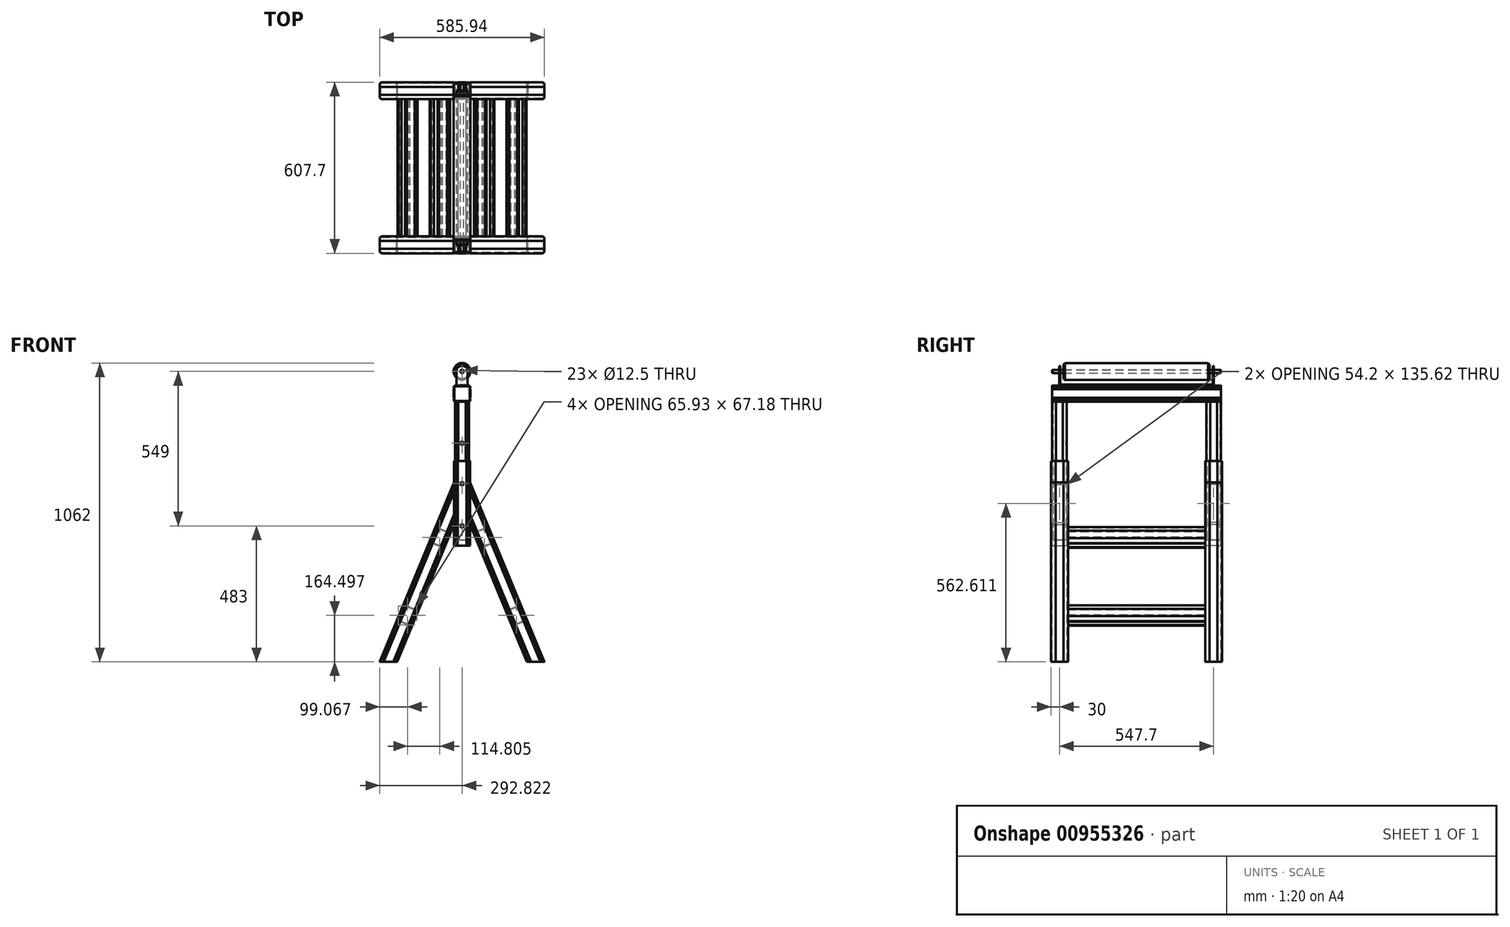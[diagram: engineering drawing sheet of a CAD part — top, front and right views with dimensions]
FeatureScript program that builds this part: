
annotation { "Feature Type Name" : "Feature", "Feature Type Description" : "" }
export const myFeature = defineFeature(function(context is Context, id is Id, definition is map)
    precondition{}
    {
        {
            var Q0;
            Q0=qCreatedBy(makeId("Front.planeOp"),FACE);
            var sketch = newSketch(context, id + "F0", { "sketchPlane" : qUnion([Q0])});
            skLineSegment(sketch, "E0", {"start": v(-264.27, 638) * mm, "end": v(0, 0) * mm});
            skLineSegment(sketch, "E1", {"start": v(0, 0) * mm, "end": v(-62.45, 0) * mm});
            skLineSegment(sketch, "E2", {"start": v(-62.45, 0) * mm, "end": v(-317.58, 615.92) * mm});
            skLineSegment(sketch, "E3", {"start": v(-317.58, 615.92) * mm, "end": v(-264.27, 638) * mm});
            skSolve(sketch);
        }
        {
            var Q0;
            Q0=makeQuery(id+"F0.imprint","IMPRINT",FACE,{"disambiguationData":[TD([[makeQuery(id+"F0.imprint","IMPRINT",EDGE,{"derivedFrom":sQuery(id+"F0.wireOp",EDGE,"E0")}),-1.0]])]});
            extrude(context, id + "F1", {"entities" : qUnion([Q0]), "depth" : 60 * mm, "offsetDistance" : 25 * mm});
        }
        {
            var Q0;
            Q0=makeQuery(id+"F1.opExtrude","CAP_EDGE",EDGE,{"disambiguationData":[OSD([sQuery(id+"F0.wireOp",EDGE,"E0")])],"isStart":false});
            var Q1;
            Q1=makeQuery(id+"F1.opExtrude","CAP_EDGE",EDGE,{"disambiguationData":[OSD([sQuery(id+"F0.wireOp",EDGE,"E0")])],"isStart":true});
            var Q2;
            Q2=makeQuery(id+"F1.opExtrude","CAP_EDGE",EDGE,{"disambiguationData":[OSD([sQuery(id+"F0.wireOp",EDGE,"E2")])],"isStart":true});
            var Q3;
            Q3=makeQuery(id+"F1.opExtrude","CAP_EDGE",EDGE,{"disambiguationData":[OSD([sQuery(id+"F0.wireOp",EDGE,"E2")])],"isStart":false});
            fillet(context, id + "F2", {"entities" : qUnion([Q0, Q1, Q2, Q3]), "radius" : 7.5 * mm, "tangentPropagation" : true, "allowEdgeOverflow" : false});
        }
        {
            var Q0;
            Q0=makeQuery(id+"F1.opExtrude","SWEPT_FACE",FACE,{"disambiguationData":[OSD([sQuery(id+"F0.wireOp",EDGE,"E3")])]});
            var sketch = newSketch(context, id + "F3", { "sketchPlane" : qUnion([Q0])});
            skArc(sketch, "E4.0", {"start": v(-50.2, -2.9) * mm, "mid": v(-53.45, -4.25) * mm, "end": v(-54.8, -7.5) * mm});
            skLineSegment(sketch, "E4.1", {"start": v(-54.8, -52.5) * mm, "end": v(-54.8, -7.5) * mm});
            skLineSegment(sketch, "E4.2", {"start": v(-50.2, -2.9) * mm, "end": v(-7.5, -2.9) * mm});
            skArc(sketch, "E4.3", {"start": v(-54.8, -52.5) * mm, "mid": v(-53.45, -55.75) * mm, "end": v(-50.2, -57.1) * mm});
            skArc(sketch, "E4.4", {"start": v(-2.9, -7.5) * mm, "mid": v(-4.25, -4.25) * mm, "end": v(-7.5, -2.9) * mm});
            skLineSegment(sketch, "E4.5", {"start": v(-2.9, -52.5) * mm, "end": v(-2.9, -7.5) * mm});
            skArc(sketch, "E4.6", {"start": v(-7.5, -57.1) * mm, "mid": v(-4.25, -55.75) * mm, "end": v(-2.9, -52.5) * mm});
            skLineSegment(sketch, "E4.7", {"start": v(-50.2, -57.1) * mm, "end": v(-7.5, -57.1) * mm});
            skLineSegment(sketch, "E5", {"start": v(-2.9, -7.5) * mm, "end": v(0, -7.5) * mm, "construction": true});
            skLineSegment(sketch, "E6", {"start": v(-2.9, -30) * mm, "end": v(0, -30) * mm, "construction": true});
            skLineSegment(sketch, "E7.0", {"start": v(-0.3, -44) * mm, "end": v(-0.3, -16) * mm});
            skLineSegment(sketch, "E8", {"start": v(-0.3, -16) * mm, "end": v(0, -16) * mm});
            skLineSegment(sketch, "E9", {"start": v(-0.3, -44) * mm, "end": v(0, -44) * mm});
            skLineSegment(sketch, "E10", {"start": v(-7.5, -57.1) * mm, "end": v(-7.5, -60) * mm, "construction": true});
            skLineSegment(sketch, "E11", {"start": v(-7.5, -60) * mm, "end": v(-8.5, -59) * mm});
            skLineSegment(sketch, "E12", {"start": v(-8.5, -59) * mm, "end": v(-9.5, -60) * mm});
            skLineSegment(sketch, "E13.1.0.0", {"start": v(-9.5, -60) * mm, "end": v(-10.5, -59) * mm});
            skLineSegment(sketch, "E13.1.0.1", {"start": v(-10.5, -59) * mm, "end": v(-11.5, -60) * mm});
            skLineSegment(sketch, "E13.2.0.0", {"start": v(-11.5, -60) * mm, "end": v(-12.5, -59) * mm});
            skLineSegment(sketch, "E13.2.0.1", {"start": v(-12.5, -59) * mm, "end": v(-13.5, -60) * mm});
            skLineSegment(sketch, "E13.direction1", {"start": v(-7.5, -60) * mm, "end": v(-9.5, -60) * mm, "construction": true});
            skLineSegment(sketch, "E14", {"start": v(-28.85, -60) * mm, "end": v(-28.85, -57.1) * mm, "construction": true});
            skLineSegment(sketch, "E15.MirrorCS", {"start": v(-50.2, -60) * mm, "end": v(-49.2, -59) * mm});
            skLineSegment(sketch, "E16.MirrorCS", {"start": v(-49.2, -59) * mm, "end": v(-48.2, -60) * mm});
            skLineSegment(sketch, "E17.MirrorCS", {"start": v(-48.2, -60) * mm, "end": v(-47.2, -59) * mm});
            skLineSegment(sketch, "E18.MirrorCS", {"start": v(-47.2, -59) * mm, "end": v(-46.2, -60) * mm});
            skLineSegment(sketch, "E19.MirrorCS", {"start": v(-46.2, -60) * mm, "end": v(-45.2, -59) * mm});
            skLineSegment(sketch, "E20.MirrorCS", {"start": v(-45.2, -59) * mm, "end": v(-44.2, -60) * mm});
            skLineSegment(sketch, "E21.MirrorCS", {"start": v(-57.4, -16) * mm, "end": v(-57.7, -16) * mm});
            skLineSegment(sketch, "E22.MirrorCS", {"start": v(-57.4, -44) * mm, "end": v(-57.4, -16) * mm});
            skLineSegment(sketch, "E23.MirrorCS", {"start": v(-57.4, -44) * mm, "end": v(-57.7, -44) * mm});
            skLineSegment(sketch, "E24.MirrorCS", {"start": v(-7.5, 0) * mm, "end": v(-8.5, -1) * mm});
            skLineSegment(sketch, "E25.MirrorCS", {"start": v(-8.5, -1) * mm, "end": v(-9.5, 0) * mm});
            skLineSegment(sketch, "E26.MirrorCS", {"start": v(-9.5, 0) * mm, "end": v(-10.5, -1) * mm});
            skLineSegment(sketch, "E27.MirrorCS", {"start": v(-10.5, -1) * mm, "end": v(-11.5, 0) * mm});
            skLineSegment(sketch, "E28.MirrorCS", {"start": v(-11.5, 0) * mm, "end": v(-12.5, -1) * mm});
            skLineSegment(sketch, "E29.MirrorCS", {"start": v(-12.5, -1) * mm, "end": v(-13.5, 0) * mm});
            skLineSegment(sketch, "E30.MirrorCS", {"start": v(-45.2, -1) * mm, "end": v(-44.2, 0) * mm});
            skLineSegment(sketch, "E31.MirrorCS", {"start": v(-46.2, 0) * mm, "end": v(-45.2, -1) * mm});
            skLineSegment(sketch, "E32.MirrorCS", {"start": v(-47.2, -1) * mm, "end": v(-46.2, 0) * mm});
            skLineSegment(sketch, "E33.MirrorCS", {"start": v(-48.2, 0) * mm, "end": v(-47.2, -1) * mm});
            skLineSegment(sketch, "E34.MirrorCS", {"start": v(-49.2, -1) * mm, "end": v(-48.2, 0) * mm});
            skLineSegment(sketch, "E35.MirrorCS", {"start": v(-50.2, 0) * mm, "end": v(-49.2, -1) * mm});
            skSolve(sketch);
        }
        {
            var Q0;
            {var subQ0=sQuery(id+"F3.wireOp",EDGE,"E24.MirrorCS");Q0=makeQuery(id+"F3.imprint","IMPRINT",FACE,{"disambiguationData":[TD([[makeQuery(id+"F3.imprint","IMPRINT",EDGE,{"derivedFrom":subQ0}),-1.0]])]});}
            var Q1;
            {var subQ0=sQuery(id+"F3.wireOp",EDGE,"E26.MirrorCS");Q1=makeQuery(id+"F3.imprint","IMPRINT",FACE,{"disambiguationData":[TD([[makeQuery(id+"F3.imprint","IMPRINT",EDGE,{"derivedFrom":subQ0}),-1.0]])]});}
            var Q2;
            {var subQ0=sQuery(id+"F3.wireOp",EDGE,"E28.MirrorCS");Q2=makeQuery(id+"F3.imprint","IMPRINT",FACE,{"disambiguationData":[TD([[makeQuery(id+"F3.imprint","IMPRINT",EDGE,{"derivedFrom":subQ0}),-1.0]])]});}
            var Q3;
            Q3=makeQuery(id+"F3.imprint","IMPRINT",FACE,{"disambiguationData":[TD([[makeQuery(id+"F3.imprint","IMPRINT",EDGE,{"derivedFrom":sQuery(id+"F3.wireOp",EDGE,"E4.0")}),1.0]])]});
            var Q4;
            {var subQ0=sQuery(id+"F3.wireOp",EDGE,"E30.MirrorCS");Q4=makeQuery(id+"F3.imprint","IMPRINT",FACE,{"disambiguationData":[TD([[makeQuery(id+"F3.imprint","IMPRINT",EDGE,{"derivedFrom":subQ0}),1.0]])]});}
            var Q5;
            {var subQ0=sQuery(id+"F3.wireOp",EDGE,"E32.MirrorCS");Q5=makeQuery(id+"F3.imprint","IMPRINT",FACE,{"disambiguationData":[TD([[makeQuery(id+"F3.imprint","IMPRINT",EDGE,{"derivedFrom":subQ0}),1.0]])]});}
            var Q6;
            {var subQ0=sQuery(id+"F3.wireOp",EDGE,"E34.MirrorCS");Q6=makeQuery(id+"F3.imprint","IMPRINT",FACE,{"disambiguationData":[TD([[makeQuery(id+"F3.imprint","IMPRINT",EDGE,{"derivedFrom":subQ0}),1.0]])]});}
            var Q7;
            {var subQ0=sQuery(id+"F3.wireOp",EDGE,"E21.MirrorCS");Q7=makeQuery(id+"F3.imprint","IMPRINT",FACE,{"disambiguationData":[TD([[makeQuery(id+"F3.imprint","IMPRINT",EDGE,{"derivedFrom":subQ0}),1.0]])]});}
            var Q8;
            {var subQ0=sQuery(id+"F3.wireOp",EDGE,"E15.MirrorCS");Q8=makeQuery(id+"F3.imprint","IMPRINT",FACE,{"disambiguationData":[TD([[makeQuery(id+"F3.imprint","IMPRINT",EDGE,{"derivedFrom":subQ0}),-1.0]])]});}
            var Q9;
            {var subQ0=sQuery(id+"F3.wireOp",EDGE,"E17.MirrorCS");Q9=makeQuery(id+"F3.imprint","IMPRINT",FACE,{"disambiguationData":[TD([[makeQuery(id+"F3.imprint","IMPRINT",EDGE,{"derivedFrom":subQ0}),-1.0]])]});}
            var Q10;
            {var subQ0=sQuery(id+"F3.wireOp",EDGE,"E19.MirrorCS");Q10=makeQuery(id+"F3.imprint","IMPRINT",FACE,{"disambiguationData":[TD([[makeQuery(id+"F3.imprint","IMPRINT",EDGE,{"derivedFrom":subQ0}),-1.0]])]});}
            var Q11;
            {var subQ0=sQuery(id+"F3.wireOp",EDGE,"E11");Q11=makeQuery(id+"F3.imprint","IMPRINT",FACE,{"disambiguationData":[TD([[makeQuery(id+"F3.imprint","IMPRINT",EDGE,{"derivedFrom":subQ0}),1.0]])]});}
            var Q12;
            {var subQ0=sQuery(id+"F3.wireOp",EDGE,"E13.1.0.0");Q12=makeQuery(id+"F3.imprint","IMPRINT",FACE,{"disambiguationData":[TD([[makeQuery(id+"F3.imprint","IMPRINT",EDGE,{"derivedFrom":subQ0}),1.0]])]});}
            var Q13;
            {var subQ0=sQuery(id+"F3.wireOp",EDGE,"E13.2.0.0");Q13=makeQuery(id+"F3.imprint","IMPRINT",FACE,{"disambiguationData":[TD([[makeQuery(id+"F3.imprint","IMPRINT",EDGE,{"derivedFrom":subQ0}),1.0]])]});}
            var Q14;
            Q14=makeQuery(id+"F3.imprint","IMPRINT",FACE,{"disambiguationData":[TD([[makeQuery(id+"F3.imprint","IMPRINT",EDGE,{"derivedFrom":sQuery(id+"F3.wireOp",EDGE,"E7.0")}),-1.0]])]});
            extrude(context, id + "F4", {"entities" : qUnion([Q0, Q1, Q2, Q3, Q4, Q5, Q6, Q7, Q8, Q9, Q10, Q11, Q12, Q13, Q14]), "operationType" : NewBodyOperationType.REMOVE, "endBound" : BoundingType.THROUGH_ALL, "oppositeDirection" : true, "depth" : 25 * mm, "offsetDistance" : 25 * mm});
        }
        {
            var Q0;
            Q0=makeQuery(id+"F1.opExtrude","CAP_FACE",FACE,{"disambiguationData":[OSD([sQuery(id+"F0.wireOp",EDGE,"E0"),sQuery(id+"F0.wireOp",EDGE,"E1"),sQuery(id+"F0.wireOp",EDGE,"E2"),sQuery(id+"F0.wireOp",EDGE,"E3")])],"isStart":false});
            var sketch = newSketch(context, id + "F5", { "sketchPlane" : qUnion([Q0])});
            skLineSegment(sketch, "E36", {"start": v(-317.58, 615.92) * mm, "end": v(-264.27, 638) * mm});
            skLineSegment(sketch, "E37", {"start": v(-264.27, 638) * mm, "end": v(-264.27, 487.22) * mm});
            skLineSegment(sketch, "E38", {"start": v(-264.27, 487.22) * mm, "end": v(-317.58, 615.92) * mm});
            skSolve(sketch);
        }
        {
            var Q0;
            Q0 = qSketchRegion(id + "F5", true);
            var Q1;
            Q1=makeQuery(id+"F1.opExtrude","CAP_FACE",FACE,{"disambiguationData":[OSD([sQuery(id+"F0.wireOp",EDGE,"E0"),sQuery(id+"F0.wireOp",EDGE,"E1"),sQuery(id+"F0.wireOp",EDGE,"E2"),sQuery(id+"F0.wireOp",EDGE,"E3")])],"isStart":true});
            extrude(context, id + "F6", {"entities" : qUnion([Q0]), "operationType" : NewBodyOperationType.REMOVE, "endBound" : BoundingType.UP_TO_SURFACE, "oppositeDirection" : true, "depth" : 25 * mm, "endBoundEntityFace" : qUnion([Q1]), "offsetDistance" : 25 * mm});
        }
        {
            var Q0;
            {var subQ0=sQuery(id+"F0.wireOp",EDGE,"E0");var subQ1=sQuery(id+"F0.wireOp",EDGE,"E3");Q0=makeQuery(id+"F6.boolean.opBoolean","MERGE",EDGE,{"derivedFrom":[makeQuery(id+"F4.boolean.opBoolean","SPLIT",EDGE,{"disambiguationData":[TD([makeQuery(id+"F4.opExtrude","SWEPT_FACE",FACE,{"disambiguationData":[OSD([sQuery(id+"F3.wireOp",EDGE,"E9")])]})])],"derivedFrom":makeQuery(id+"F1.opExtrude","SWEPT_EDGE",EDGE,{"disambiguationData":[OSD([subQ0,subQ1])]})})],"fromTools":[makeQuery(id+"F6.opExtrude","SWEPT_EDGE",EDGE,{"disambiguationData":[OSD([sQuery(id+"F5.wireOp",EDGE,"E36"),sQuery(id+"F5.wireOp",EDGE,"E37")])]})]});}
            cPlane(context, id + "F7", {"entities" : qUnion([Q0]), "cplaneType" : CPlaneType.LINE_ANGLE, "offset" : 25 * mm, "angle" : 0 * degree, "width" : 150 * mm, "height" : 150 * mm});
        }
        {
            var Q0;
            Q0=qCreatedBy(id+"F7.planeOp",FACE);
            cPlane(context, id + "F8", {"entities" : qUnion([Q0]), "cplaneType" : CPlaneType.OFFSET, "offset" : 75 * mm, "width" : 150 * mm, "height" : 150 * mm});
        }
        {
            var Q0;
            Q0=qCreatedBy(id+"F8.planeOp",FACE);
            var sketch = newSketch(context, id + "F9", { "sketchPlane" : qUnion([Q0])});
            skLineSegment(sketch, "E39", {"start": v(-321.97, -52.5) * mm, "end": v(-321.97, -44) * mm});
            skLineSegment(sketch, "E40", {"start": v(-321.97, -44) * mm, "end": v(-321.67, -44) * mm});
            skLineSegment(sketch, "E41", {"start": v(-321.67, -44) * mm, "end": v(-321.67, -30) * mm});
            skLineSegment(sketch, "E42", {"start": v(-321.67, -30) * mm, "end": v(-264.57, -30) * mm, "construction": true});
            skLineSegment(sketch, "E43", {"start": v(-264.57, -30) * mm, "end": v(-264.57, -44) * mm});
            skLineSegment(sketch, "E44", {"start": v(-264.57, -44) * mm, "end": v(-264.27, -44) * mm});
            skLineSegment(sketch, "E45", {"start": v(-264.27, -44) * mm, "end": v(-264.27, -52.5) * mm});
            skArc(sketch, "E46.filletArc", {"start": v(-271.77, -60) * mm, "mid": v(-266.46, -57.8) * mm, "end": v(-264.27, -52.5) * mm});
            skArc(sketch, "E47.filletArc", {"start": v(-321.97, -52.5) * mm, "mid": v(-319.77, -57.8) * mm, "end": v(-314.47, -60) * mm});
            skLineSegment(sketch, "E48", {"start": v(-277.77, -60) * mm, "end": v(-308.47, -60) * mm});
            skLineSegment(sketch, "E49", {"start": v(-271.77, -60) * mm, "end": v(-272.77, -59) * mm});
            skLineSegment(sketch, "E50", {"start": v(-272.77, -59) * mm, "end": v(-273.77, -60) * mm});
            skLineSegment(sketch, "E51.1.0.0", {"start": v(-273.77, -60) * mm, "end": v(-274.77, -59) * mm});
            skLineSegment(sketch, "E51.1.0.1", {"start": v(-274.77, -59) * mm, "end": v(-275.77, -60) * mm});
            skLineSegment(sketch, "E51.2.0.0", {"start": v(-275.77, -60) * mm, "end": v(-276.77, -59) * mm});
            skLineSegment(sketch, "E51.2.0.1", {"start": v(-276.77, -59) * mm, "end": v(-277.77, -60) * mm});
            skLineSegment(sketch, "E51.direction1", {"start": v(-271.77, -60) * mm, "end": v(-273.77, -60) * mm, "construction": true});
            skLineSegment(sketch, "E52", {"start": v(-314.47, -60) * mm, "end": v(-313.47, -59) * mm});
            skLineSegment(sketch, "E53", {"start": v(-313.47, -59) * mm, "end": v(-312.47, -60) * mm});
            skLineSegment(sketch, "E54.1.0.0", {"start": v(-312.47, -60) * mm, "end": v(-311.47, -59) * mm});
            skLineSegment(sketch, "E54.1.0.1", {"start": v(-311.47, -59) * mm, "end": v(-310.47, -60) * mm});
            skLineSegment(sketch, "E54.2.0.0", {"start": v(-310.47, -60) * mm, "end": v(-309.47, -59) * mm});
            skLineSegment(sketch, "E54.2.0.1", {"start": v(-309.47, -59) * mm, "end": v(-308.47, -60) * mm});
            skLineSegment(sketch, "E54.direction1", {"start": v(-314.47, -60) * mm, "end": v(-312.47, -60) * mm, "construction": true});
            skLineSegment(sketch, "E55", {"start": v(-318.77, -30) * mm, "end": v(-318.77, -52.6) * mm});
            skLineSegment(sketch, "E56", {"start": v(-314.27, -57.1) * mm, "end": v(-271.67, -57.1) * mm});
            skLineSegment(sketch, "E57", {"start": v(-267.17, -52.6) * mm, "end": v(-267.17, -30) * mm});
            skPoint(sketch, "E58.visualSharp", {"position": v(-318.77, -57.1) * mm});
            skArc(sketch, "E58.filletArc", {"start": v(-318.77, -52.6) * mm, "mid": v(-317.45, -55.78) * mm, "end": v(-314.27, -57.1) * mm});
            skPoint(sketch, "E59.visualSharp", {"position": v(-267.17, -57.1) * mm});
            skArc(sketch, "E59.filletArc", {"start": v(-271.67, -57.1) * mm, "mid": v(-268.49, -55.78) * mm, "end": v(-267.17, -52.6) * mm});
            skLineSegment(sketch, "E60.MirrorCS", {"start": v(-314.47, 0) * mm, "end": v(-312.47, 0) * mm, "construction": true});
            skLineSegment(sketch, "E61.MirrorCS", {"start": v(-313.47, -1) * mm, "end": v(-312.47, 0) * mm});
            skLineSegment(sketch, "E62.MirrorCS", {"start": v(-314.47, 0) * mm, "end": v(-313.47, -1) * mm});
            skLineSegment(sketch, "E63.MirrorCS", {"start": v(-264.57, -16) * mm, "end": v(-264.27, -16) * mm});
            skLineSegment(sketch, "E64.MirrorCS", {"start": v(-271.77, 0) * mm, "end": v(-272.77, -1) * mm});
            skLineSegment(sketch, "E65.MirrorCS", {"start": v(-273.77, 0) * mm, "end": v(-274.77, -1) * mm});
            skLineSegment(sketch, "E66.MirrorCS", {"start": v(-271.77, 0) * mm, "end": v(-273.77, 0) * mm, "construction": true});
            skLineSegment(sketch, "E67.MirrorCS", {"start": v(-312.47, 0) * mm, "end": v(-311.47, -1) * mm});
            skLineSegment(sketch, "E68.MirrorCS", {"start": v(-272.77, -1) * mm, "end": v(-273.77, 0) * mm});
            skLineSegment(sketch, "E69.MirrorCS", {"start": v(-321.97, -16) * mm, "end": v(-321.67, -16) * mm});
            skLineSegment(sketch, "E70.MirrorCS", {"start": v(-309.47, -1) * mm, "end": v(-308.47, 0) * mm});
            skLineSegment(sketch, "E71.MirrorCS", {"start": v(-276.77, -1) * mm, "end": v(-277.77, 0) * mm});
            skLineSegment(sketch, "E72.MirrorCS", {"start": v(-275.77, 0) * mm, "end": v(-276.77, -1) * mm});
            skLineSegment(sketch, "E73.MirrorCS", {"start": v(-310.47, 0) * mm, "end": v(-309.47, -1) * mm});
            skLineSegment(sketch, "E74.MirrorCS", {"start": v(-274.77, -1) * mm, "end": v(-275.77, 0) * mm});
            skLineSegment(sketch, "E75.MirrorCS", {"start": v(-311.47, -1) * mm, "end": v(-310.47, 0) * mm});
            skLineSegment(sketch, "E76.MirrorCS", {"start": v(-318.77, -30) * mm, "end": v(-318.77, -7.4) * mm});
            skArc(sketch, "E77.MirrorCS", {"start": v(-271.67, -2.9) * mm, "mid": v(-268.49, -4.22) * mm, "end": v(-267.17, -7.4) * mm});
            skArc(sketch, "E78.MirrorCS", {"start": v(-318.77, -7.4) * mm, "mid": v(-317.45, -4.22) * mm, "end": v(-314.27, -2.9) * mm});
            skPoint(sketch, "E79.MirrorP", {"position": v(-318.77, -2.9) * mm});
            skArc(sketch, "E80.MirrorCS", {"start": v(-271.77, 0) * mm, "mid": v(-266.46, -2.2) * mm, "end": v(-264.27, -7.5) * mm});
            skLineSegment(sketch, "E81.MirrorCS", {"start": v(-267.17, -7.4) * mm, "end": v(-267.17, -30) * mm});
            skLineSegment(sketch, "E82.MirrorCS", {"start": v(-321.67, -16) * mm, "end": v(-321.67, -30) * mm});
            skLineSegment(sketch, "E83.MirrorCS", {"start": v(-264.27, -16) * mm, "end": v(-264.27, -7.5) * mm});
            skPoint(sketch, "E84.MirrorP", {"position": v(-267.17, -2.9) * mm});
            skLineSegment(sketch, "E85.MirrorCS", {"start": v(-264.57, -30) * mm, "end": v(-264.57, -16) * mm});
            skLineSegment(sketch, "E86.MirrorCS", {"start": v(-314.27, -2.9) * mm, "end": v(-271.67, -2.9) * mm});
            skLineSegment(sketch, "E87.MirrorCS", {"start": v(-321.97, -7.5) * mm, "end": v(-321.97, -16) * mm});
            skArc(sketch, "E88.MirrorCS", {"start": v(-321.97, -7.5) * mm, "mid": v(-319.77, -2.2) * mm, "end": v(-314.47, 0) * mm});
            skLineSegment(sketch, "E89.MirrorCS", {"start": v(-277.77, 0) * mm, "end": v(-308.47, 0) * mm});
            skSolve(sketch);
        }
        {
            var Q0;
            Q0 = qSketchRegion(id + "F9", true);
            extrude(context, id + "F10", {"entities" : qUnion([Q0]), "oppositeDirection" : true, "depth" : 300 * mm, "offsetDistance" : 25 * mm});
        }
        {
            var Q0;
            Q0=makeQuery(id+"F10.opExtrude","SWEPT_FACE",FACE,{"disambiguationData":[OSD([sQuery(id+"F9.wireOp",EDGE,"E57"),sQuery(id+"F9.wireOp",EDGE,"E81.MirrorCS")])]});
            var Q1;
            Q1=makeQuery(id+"F10.opExtrude","SWEPT_FACE",FACE,{"disambiguationData":[OSD([sQuery(id+"F9.wireOp",EDGE,"E55"),sQuery(id+"F9.wireOp",EDGE,"E76.MirrorCS")])]});
            cPlane(context, id + "F11", {"entities" : qUnion([Q0, Q1]), "cplaneType" : CPlaneType.MID_PLANE, "offset" : 25 * mm, "width" : 150 * mm, "height" : 150 * mm});
        }
        {
            var Q0;
            Q0=makeQuery(id+"F1.opExtrude","SWEPT_BODY",BODY,{"disambiguationData":[OSD([sQuery(id+"F0.wireOp",EDGE,"E0"),sQuery(id+"F0.wireOp",EDGE,"E1"),sQuery(id+"F0.wireOp",EDGE,"E2"),sQuery(id+"F0.wireOp",EDGE,"E3")])]});
            var Q1;
            Q1=qCreatedBy(id+"F11.planeOp",FACE);
            mirror(context, id + "F12", {"entities" : qUnion([Q0]), "mirrorPlane" : qUnion([Q1])});
        }
        {
            var Q0;
            Q0=makeQuery(id+"F10.opExtrude","SWEPT_FACE",FACE,{"disambiguationData":[OSD([sQuery(id+"F9.wireOp",EDGE,"E89.MirrorCS")])]});
            var sketch = newSketch(context, id + "F13", { "sketchPlane" : qUnion([Q0])});
            skLineSegment(sketch, "E90", {"start": v(293.12, 713) * mm, "end": v(293.12, 413) * mm, "construction": true});
            skCircle(sketch, "E91", {"center": v(293.12, 633) * mm, "radius": 6.25 * mm});
            skCircle(sketch, "E92", {"center": v(293.12, 483) * mm, "radius": 6.25 * mm});
            skSolve(sketch);
        }
        {
            var Q0;
            Q0 = qSketchRegion(id + "F13", true);
            var Q1;
            Q1=makeQuery(id+"F10.opExtrude","SWEPT_FACE",FACE,{"disambiguationData":[OSD([sQuery(id+"F9.wireOp",EDGE,"E48")])]});
            extrude(context, id + "F14", {"entities" : qUnion([Q0]), "operationType" : NewBodyOperationType.REMOVE, "endBound" : BoundingType.UP_TO_SURFACE, "oppositeDirection" : true, "depth" : 25 * mm, "endBoundEntityFace" : qUnion([Q1]), "offsetDistance" : 25 * mm});
        }
        {
            var Q0;
            Q0=makeQuery(id+"F14.boolean.opBoolean","COPY",FACE,{"disambiguationData":[TD([makeQuery(id+"F10.opExtrude","SWEPT_FACE",FACE,{"disambiguationData":[OSD([sQuery(id+"F9.wireOp",EDGE,"E48")])]})])],"derivedFrom":makeQuery(id+"F14.opExtrude","SWEPT_FACE",FACE,{"disambiguationData":[OSD([sQuery(id+"F13.wireOp",EDGE,"E92")])]})});
            cPlane(context, id + "F15", {"entities" : qUnion([Q0]), "cplaneType" : CPlaneType.LINE_ANGLE, "offset" : 25 * mm, "angle" : 0 * degree, "width" : 150 * mm, "height" : 150 * mm});
        }
        {
            var Q0;
            Q0=qCreatedBy(id+"F15.planeOp",FACE);
            cPlane(context, id + "F16", {"entities" : qUnion([Q0]), "cplaneType" : CPlaneType.OFFSET, "offset" : 50 * mm, "width" : 150 * mm, "height" : 150 * mm});
        }
        {
            var Q0;
            Q0=qCreatedBy(id+"F16.planeOp",FACE);
            var sketch = newSketch(context, id + "F17", { "sketchPlane" : qUnion([Q0])});
            skLineSegment(sketch, "E93", {"start": v(-293.12, 0) * mm, "end": v(-293.12, 60) * mm, "construction": true});
            skLineSegment(sketch, "E94", {"start": v(-293.12, 56.15) * mm, "end": v(-306.87, 56.15) * mm});
            skLineSegment(sketch, "E95", {"start": v(-318.37, 48.65) * mm, "end": v(-318.37, 42.15) * mm});
            skLineSegment(sketch, "E96", {"start": v(-306.87, 3.85) * mm, "end": v(-293.12, 3.85) * mm});
            skPoint(sketch, "E97.visualSharp", {"position": v(-318.37, 56.15) * mm});
            skArc(sketch, "E97.filletArc", {"start": v(-310.87, 56.15) * mm, "mid": v(-316.17, 53.95) * mm, "end": v(-318.37, 48.65) * mm});
            skPoint(sketch, "E98.visualSharp", {"position": v(-318.37, 3.85) * mm});
            skArc(sketch, "E98.filletArc", {"start": v(-318.37, 11.35) * mm, "mid": v(-316.17, 6.05) * mm, "end": v(-310.87, 3.85) * mm});
            skLineSegment(sketch, "E99", {"start": v(-310.87, 56.15) * mm, "end": v(-309.87, 55.15) * mm});
            skLineSegment(sketch, "E100", {"start": v(-309.87, 55.15) * mm, "end": v(-308.87, 56.15) * mm});
            skLineSegment(sketch, "E101.1.0.0", {"start": v(-308.87, 56.15) * mm, "end": v(-307.87, 55.15) * mm});
            skLineSegment(sketch, "E101.1.0.1", {"start": v(-307.87, 55.15) * mm, "end": v(-306.87, 56.15) * mm});
            skLineSegment(sketch, "E101.direction1", {"start": v(-309.87, 55.15) * mm, "end": v(-307.87, 55.15) * mm, "construction": true});
            skLineSegment(sketch, "E102", {"start": v(-310.87, 3.85) * mm, "end": v(-309.87, 4.85) * mm});
            skLineSegment(sketch, "E103", {"start": v(-309.87, 4.85) * mm, "end": v(-308.87, 3.85) * mm});
            skLineSegment(sketch, "E104.1.0.0", {"start": v(-308.87, 3.85) * mm, "end": v(-307.87, 4.85) * mm});
            skLineSegment(sketch, "E104.1.0.1", {"start": v(-307.87, 4.85) * mm, "end": v(-306.87, 3.85) * mm});
            skLineSegment(sketch, "E104.direction1", {"start": v(-310.87, 3.85) * mm, "end": v(-308.87, 3.85) * mm, "construction": true});
            skLineSegment(sketch, "E105", {"start": v(-293.12, 53.25) * mm, "end": v(-310.97, 53.25) * mm});
            skLineSegment(sketch, "E106", {"start": v(-315.47, 48.75) * mm, "end": v(-315.47, 11.25) * mm});
            skLineSegment(sketch, "E107", {"start": v(-310.97, 6.75) * mm, "end": v(-293.12, 6.75) * mm});
            skPoint(sketch, "E108.visualSharp", {"position": v(-315.47, 53.25) * mm});
            skArc(sketch, "E108.filletArc", {"start": v(-310.97, 53.25) * mm, "mid": v(-314.15, 51.93) * mm, "end": v(-315.47, 48.75) * mm});
            skPoint(sketch, "E109.visualSharp", {"position": v(-315.47, 6.75) * mm});
            skArc(sketch, "E109.filletArc", {"start": v(-315.47, 11.25) * mm, "mid": v(-314.15, 8.07) * mm, "end": v(-310.97, 6.75) * mm});
            skLineSegment(sketch, "E110", {"start": v(-306.87, 0) * mm, "end": v(-306.87, 56.15) * mm, "construction": true});
            skLineSegment(sketch, "E111", {"start": v(-306.87, 60) * mm, "end": v(-306.87, 3.85) * mm, "construction": true});
            skLineSegment(sketch, "E112.MirrorCS", {"start": v(-275.37, 3.85) * mm, "end": v(-277.37, 3.85) * mm, "construction": true});
            skLineSegment(sketch, "E113.MirrorCS", {"start": v(-275.37, 56.15) * mm, "end": v(-276.37, 55.15) * mm});
            skLineSegment(sketch, "E114.MirrorCS", {"start": v(-277.37, 3.85) * mm, "end": v(-278.37, 4.85) * mm});
            skLineSegment(sketch, "E115.MirrorCS", {"start": v(-276.37, 55.15) * mm, "end": v(-278.37, 55.15) * mm, "construction": true});
            skLineSegment(sketch, "E116.MirrorCS", {"start": v(-276.37, 55.15) * mm, "end": v(-277.37, 56.15) * mm});
            skLineSegment(sketch, "E117.MirrorCS", {"start": v(-278.37, 55.15) * mm, "end": v(-279.37, 56.15) * mm});
            skLineSegment(sketch, "E118.MirrorCS", {"start": v(-278.37, 4.85) * mm, "end": v(-279.37, 3.85) * mm});
            skLineSegment(sketch, "E119.MirrorCS", {"start": v(-277.37, 56.15) * mm, "end": v(-278.37, 55.15) * mm});
            skLineSegment(sketch, "E120.MirrorCS", {"start": v(-276.37, 4.85) * mm, "end": v(-277.37, 3.85) * mm});
            skLineSegment(sketch, "E121.MirrorCS", {"start": v(-275.37, 3.85) * mm, "end": v(-276.37, 4.85) * mm});
            skLineSegment(sketch, "E122.MirrorCS", {"start": v(-279.37, 60) * mm, "end": v(-279.37, 3.85) * mm, "construction": true});
            skLineSegment(sketch, "E123.MirrorCS", {"start": v(-279.37, 0) * mm, "end": v(-279.37, 56.15) * mm, "construction": true});
            skLineSegment(sketch, "E124.MirrorCS", {"start": v(-293.12, 56.15) * mm, "end": v(-279.37, 56.15) * mm});
            skLineSegment(sketch, "E125.MirrorCS", {"start": v(-267.87, 48.65) * mm, "end": v(-267.87, 42.15) * mm});
            skPoint(sketch, "E126.MirrorP", {"position": v(-267.87, 56.15) * mm});
            skArc(sketch, "E127.MirrorCS", {"start": v(-270.77, 11.25) * mm, "mid": v(-272.09, 8.07) * mm, "end": v(-275.27, 6.75) * mm});
            skArc(sketch, "E128.MirrorCS", {"start": v(-267.87, 11.35) * mm, "mid": v(-270.06, 6.05) * mm, "end": v(-275.37, 3.85) * mm});
            skArc(sketch, "E129.MirrorCS", {"start": v(-275.37, 56.15) * mm, "mid": v(-270.06, 53.95) * mm, "end": v(-267.87, 48.65) * mm});
            skLineSegment(sketch, "E130.MirrorCS", {"start": v(-275.27, 6.75) * mm, "end": v(-293.12, 6.75) * mm});
            skPoint(sketch, "E131.MirrorP", {"position": v(-267.87, 3.85) * mm});
            skPoint(sketch, "E132.MirrorP", {"position": v(-270.77, 6.75) * mm});
            skPoint(sketch, "E133.MirrorP", {"position": v(-270.77, 53.25) * mm});
            skArc(sketch, "E134.MirrorCS", {"start": v(-275.27, 53.25) * mm, "mid": v(-272.09, 51.93) * mm, "end": v(-270.77, 48.75) * mm});
            skLineSegment(sketch, "E135.MirrorCS", {"start": v(-293.12, 53.25) * mm, "end": v(-275.27, 53.25) * mm});
            skLineSegment(sketch, "E136.MirrorCS", {"start": v(-270.77, 48.75) * mm, "end": v(-270.77, 11.25) * mm});
            skLineSegment(sketch, "E137.MirrorCS", {"start": v(-279.37, 3.85) * mm, "end": v(-293.12, 3.85) * mm});
            skLineSegment(sketch, "E138", {"start": v(-318.37, 17.85) * mm, "end": v(-318.12, 17.85) * mm});
            skLineSegment(sketch, "E139", {"start": v(-318.12, 17.85) * mm, "end": v(-318.12, 42.15) * mm});
            skLineSegment(sketch, "E140", {"start": v(-318.12, 42.15) * mm, "end": v(-318.37, 42.15) * mm});
            skLineSegment(sketch, "E141.trimOffspring", {"start": v(-318.37, 17.85) * mm, "end": v(-318.37, 11.35) * mm});
            skLineSegment(sketch, "E142.MirrorCS", {"start": v(-267.87, 17.85) * mm, "end": v(-268.12, 17.85) * mm});
            skLineSegment(sketch, "E143.MirrorCS", {"start": v(-268.12, 17.85) * mm, "end": v(-268.12, 42.15) * mm});
            skLineSegment(sketch, "E144.MirrorCS", {"start": v(-268.12, 42.15) * mm, "end": v(-267.87, 42.15) * mm});
            skLineSegment(sketch, "E145.trimOffspring", {"start": v(-267.87, 17.85) * mm, "end": v(-267.87, 11.35) * mm});
            skSolve(sketch);
        }
        {
            var Q0;
            Q0 = qSketchRegion(id + "F17", true);
            extrude(context, id + "F18", {"entities" : qUnion([Q0]), "oppositeDirection" : true, "depth" : 491.3 * mm, "offsetDistance" : 25 * mm});
        }
        {
            var Q0;
            Q0=makeQuery(id+"F18.opExtrude","SWEPT_FACE",FACE,{"disambiguationData":[OSD([sQuery(id+"F17.wireOp",EDGE,"E96"),sQuery(id+"F17.wireOp",EDGE,"E137.MirrorCS")])]});
            var sketch = newSketch(context, id + "F19", { "sketchPlane" : qUnion([Q0])});
            skCircle(sketch, "E146", {"center": v(293.12, 633) * mm, "radius": 6.25 * mm});
            skCircle(sketch, "E147", {"center": v(293.12, 483) * mm, "radius": 6.25 * mm});
            skCircle(sketch, "E148", {"center": v(293.12, 776.75) * mm, "radius": 6.25 * mm});
            skSolve(sketch);
        }
        {
            var Q0;
            Q0 = qSketchRegion(id + "F19", true);
            var Q1;
            Q1=makeQuery(id+"F18.opExtrude","SWEPT_FACE",FACE,{"disambiguationData":[OSD([sQuery(id+"F17.wireOp",EDGE,"E94"),sQuery(id+"F17.wireOp",EDGE,"E124.MirrorCS")])]});
            extrude(context, id + "F20", {"entities" : qUnion([Q0]), "operationType" : NewBodyOperationType.REMOVE, "endBound" : BoundingType.UP_TO_SURFACE, "oppositeDirection" : true, "depth" : 25 * mm, "endBoundEntityFace" : qUnion([Q1]), "offsetDistance" : 25 * mm});
        }
        {
            var Q0;
            Q0=makeQuery(id+"F18.opExtrude","SWEPT_FACE",FACE,{"disambiguationData":[OSD([sQuery(id+"F17.wireOp",EDGE,"E96"),sQuery(id+"F17.wireOp",EDGE,"E137.MirrorCS")])]});
            var sketch = newSketch(context, id + "F21", { "sketchPlane" : qUnion([Q0])});
            skLineSegment(sketch, "E149", {"start": v(293.12, 981.7) * mm, "end": v(293.12, 924.6) * mm, "construction": true});
            skLineSegment(sketch, "E150", {"start": v(279.12, 982) * mm, "end": v(270.62, 982) * mm});
            skLineSegment(sketch, "E151", {"start": v(263.12, 968.5) * mm, "end": v(263.12, 937.8) * mm});
            skLineSegment(sketch, "E152", {"start": v(270.62, 924.3) * mm, "end": v(279.12, 924.3) * mm});
            skPoint(sketch, "E153.visualSharp", {"position": v(263.12, 982) * mm});
            skArc(sketch, "E153.filletArc", {"start": v(270.62, 982) * mm, "mid": v(265.31, 979.8) * mm, "end": v(263.12, 974.5) * mm});
            skPoint(sketch, "E154.visualSharp", {"position": v(263.12, 924.3) * mm});
            skArc(sketch, "E154.filletArc", {"start": v(263.12, 931.8) * mm, "mid": v(265.31, 926.5) * mm, "end": v(270.62, 924.3) * mm});
            skLineSegment(sketch, "E155", {"start": v(263.12, 974.5) * mm, "end": v(264.12, 973.5) * mm});
            skLineSegment(sketch, "E156", {"start": v(264.12, 973.5) * mm, "end": v(263.12, 972.5) * mm});
            skLineSegment(sketch, "E157.0.1.0", {"start": v(263.12, 972.5) * mm, "end": v(264.12, 971.5) * mm});
            skLineSegment(sketch, "E157.0.1.1", {"start": v(264.12, 971.5) * mm, "end": v(263.12, 970.5) * mm});
            skLineSegment(sketch, "E157.0.2.0", {"start": v(263.12, 970.5) * mm, "end": v(264.12, 969.5) * mm});
            skLineSegment(sketch, "E157.0.2.1", {"start": v(264.12, 969.5) * mm, "end": v(263.12, 968.5) * mm});
            skLineSegment(sketch, "E157.direction1", {"start": v(264.12, 973.5) * mm, "end": v(289.12, 973.5) * mm, "construction": true});
            skLineSegment(sketch, "E157.direction2", {"start": v(264.12, 973.5) * mm, "end": v(264.12, 971.5) * mm, "construction": true});
            skLineSegment(sketch, "E158", {"start": v(263.12, 931.8) * mm, "end": v(264.12, 932.8) * mm});
            skLineSegment(sketch, "E159", {"start": v(264.12, 932.8) * mm, "end": v(263.12, 933.8) * mm});
            skLineSegment(sketch, "E160.0.1.0", {"start": v(263.12, 933.8) * mm, "end": v(264.12, 934.8) * mm});
            skLineSegment(sketch, "E160.0.1.1", {"start": v(264.12, 934.8) * mm, "end": v(263.12, 935.8) * mm});
            skLineSegment(sketch, "E160.0.2.0", {"start": v(263.12, 935.8) * mm, "end": v(264.12, 936.8) * mm});
            skLineSegment(sketch, "E160.0.2.1", {"start": v(264.12, 936.8) * mm, "end": v(263.12, 937.8) * mm});
            skLineSegment(sketch, "E160.direction1", {"start": v(263.12, 931.8) * mm, "end": v(288.12, 931.8) * mm, "construction": true});
            skLineSegment(sketch, "E160.direction2", {"start": v(263.12, 931.8) * mm, "end": v(263.12, 933.8) * mm, "construction": true});
            skLineSegment(sketch, "E161", {"start": v(293.12, 981.7) * mm, "end": v(279.12, 981.7) * mm});
            skLineSegment(sketch, "E162", {"start": v(279.12, 981.7) * mm, "end": v(279.12, 982) * mm});
            skLineSegment(sketch, "E163", {"start": v(293.12, 924.6) * mm, "end": v(279.12, 924.6) * mm});
            skLineSegment(sketch, "E164", {"start": v(279.12, 924.6) * mm, "end": v(279.12, 924.3) * mm});
            skPoint(sketch, "E165.orphan", {"position": v(293.12, 924.3) * mm});
            skPoint(sketch, "E166.orphan", {"position": v(293.12, 982) * mm});
            skLineSegment(sketch, "E167", {"start": v(266.02, 974.3) * mm, "end": v(266.02, 932) * mm});
            skLineSegment(sketch, "E168", {"start": v(270.52, 927.5) * mm, "end": v(293.12, 927.5) * mm});
            skLineSegment(sketch, "E169", {"start": v(270.52, 978.8) * mm, "end": v(293.12, 978.8) * mm});
            skPoint(sketch, "E170.visualSharp", {"position": v(266.02, 978.8) * mm});
            skArc(sketch, "E170.filletArc", {"start": v(270.52, 978.8) * mm, "mid": v(267.34, 977.48) * mm, "end": v(266.02, 974.3) * mm});
            skPoint(sketch, "E171.visualSharp", {"position": v(266.02, 927.5) * mm});
            skArc(sketch, "E171.filletArc", {"start": v(266.02, 932) * mm, "mid": v(267.34, 928.82) * mm, "end": v(270.52, 927.5) * mm});
            skLineSegment(sketch, "E172.MirrorCS", {"start": v(322.12, 932.8) * mm, "end": v(323.12, 933.8) * mm});
            skLineSegment(sketch, "E173.MirrorCS", {"start": v(323.12, 931.8) * mm, "end": v(323.12, 933.8) * mm, "construction": true});
            skLineSegment(sketch, "E174.MirrorCS", {"start": v(322.12, 971.5) * mm, "end": v(323.12, 970.5) * mm});
            skLineSegment(sketch, "E175.MirrorCS", {"start": v(323.12, 931.8) * mm, "end": v(322.12, 932.8) * mm});
            skLineSegment(sketch, "E176.MirrorCS", {"start": v(323.12, 933.8) * mm, "end": v(322.12, 934.8) * mm});
            skLineSegment(sketch, "E177.MirrorCS", {"start": v(307.12, 981.7) * mm, "end": v(307.12, 982) * mm});
            skLineSegment(sketch, "E178.MirrorCS", {"start": v(322.12, 969.5) * mm, "end": v(323.12, 968.5) * mm});
            skLineSegment(sketch, "E179.MirrorCS", {"start": v(323.12, 972.5) * mm, "end": v(322.12, 971.5) * mm});
            skLineSegment(sketch, "E180.MirrorCS", {"start": v(322.12, 973.5) * mm, "end": v(323.12, 972.5) * mm});
            skLineSegment(sketch, "E181.MirrorCS", {"start": v(322.12, 973.5) * mm, "end": v(322.12, 971.5) * mm, "construction": true});
            skLineSegment(sketch, "E182.MirrorCS", {"start": v(323.12, 970.5) * mm, "end": v(322.12, 969.5) * mm});
            skLineSegment(sketch, "E183.MirrorCS", {"start": v(323.12, 974.5) * mm, "end": v(322.12, 973.5) * mm});
            skLineSegment(sketch, "E184.MirrorCS", {"start": v(323.12, 935.8) * mm, "end": v(322.12, 936.8) * mm});
            skLineSegment(sketch, "E185.MirrorCS", {"start": v(322.12, 934.8) * mm, "end": v(323.12, 935.8) * mm});
            skArc(sketch, "E186.MirrorCS", {"start": v(315.72, 978.8) * mm, "mid": v(318.9, 977.48) * mm, "end": v(320.22, 974.3) * mm});
            skLineSegment(sketch, "E187.MirrorCS", {"start": v(322.12, 936.8) * mm, "end": v(323.12, 937.8) * mm});
            skArc(sketch, "E188.MirrorCS", {"start": v(320.22, 932) * mm, "mid": v(318.9, 928.82) * mm, "end": v(315.72, 927.5) * mm});
            skLineSegment(sketch, "E189.MirrorCS", {"start": v(307.12, 924.6) * mm, "end": v(307.12, 924.3) * mm});
            skArc(sketch, "E190.MirrorCS", {"start": v(323.12, 931.8) * mm, "mid": v(320.92, 926.5) * mm, "end": v(315.62, 924.3) * mm});
            skArc(sketch, "E191.MirrorCS", {"start": v(315.62, 982) * mm, "mid": v(320.92, 979.8) * mm, "end": v(323.12, 974.5) * mm});
            skLineSegment(sketch, "E192.MirrorCS", {"start": v(322.12, 973.5) * mm, "end": v(297.12, 973.5) * mm, "construction": true});
            skPoint(sketch, "E193.MirrorP", {"position": v(320.22, 927.5) * mm});
            skLineSegment(sketch, "E194.MirrorCS", {"start": v(315.72, 927.5) * mm, "end": v(293.12, 927.5) * mm});
            skLineSegment(sketch, "E195.MirrorCS", {"start": v(320.22, 974.3) * mm, "end": v(320.22, 932) * mm});
            skLineSegment(sketch, "E196.MirrorCS", {"start": v(293.12, 981.7) * mm, "end": v(307.12, 981.7) * mm});
            skLineSegment(sketch, "E197.MirrorCS", {"start": v(323.12, 968.5) * mm, "end": v(323.12, 937.8) * mm});
            skLineSegment(sketch, "E198.MirrorCS", {"start": v(323.12, 931.8) * mm, "end": v(298.12, 931.8) * mm, "construction": true});
            skLineSegment(sketch, "E199.MirrorCS", {"start": v(315.62, 924.3) * mm, "end": v(307.12, 924.3) * mm});
            skPoint(sketch, "E200.MirrorP", {"position": v(323.12, 982) * mm});
            skLineSegment(sketch, "E201.MirrorCS", {"start": v(307.12, 982) * mm, "end": v(315.62, 982) * mm});
            skLineSegment(sketch, "E202.MirrorCS", {"start": v(293.12, 924.6) * mm, "end": v(307.12, 924.6) * mm});
            skLineSegment(sketch, "E203.MirrorCS", {"start": v(315.72, 978.8) * mm, "end": v(293.12, 978.8) * mm});
            skPoint(sketch, "E204.MirrorP", {"position": v(320.22, 978.8) * mm});
            skPoint(sketch, "E205.MirrorP", {"position": v(323.12, 924.3) * mm});
            skSolve(sketch);
        }
        {
            var Q0;
            Q0=makeQuery(id+"F21.imprint","IMPRINT",FACE,{"disambiguationData":[TD([[makeQuery(id+"F21.imprint","IMPRINT",EDGE,{"derivedFrom":sQuery(id+"F21.wireOp",EDGE,"E150")}),1.0]])]});
            extrude(context, id + "F22", {"entities" : qUnion([Q0]), "oppositeDirection" : true, "depth" : 600 * mm, "offsetDistance" : 25 * mm});
        }
        {
            var Q0;
            Q0=makeQuery(id+"F22.opExtrude","CAP_FACE",FACE,{"disambiguationData":[OSD([sQuery(id+"F21.wireOp",EDGE,"E150"),sQuery(id+"F21.wireOp",EDGE,"E151"),sQuery(id+"F21.wireOp",EDGE,"E152"),sQuery(id+"F21.wireOp",EDGE,"E153.filletArc"),sQuery(id+"F21.wireOp",EDGE,"E154.filletArc"),sQuery(id+"F21.wireOp",EDGE,"E155"),sQuery(id+"F21.wireOp",EDGE,"E156"),sQuery(id+"F21.wireOp",EDGE,"E157.0.1.0"),sQuery(id+"F21.wireOp",EDGE,"E157.0.1.1"),sQuery(id+"F21.wireOp",EDGE,"E157.0.2.0"),sQuery(id+"F21.wireOp",EDGE,"E157.0.2.1"),sQuery(id+"F21.wireOp",EDGE,"E158"),sQuery(id+"F21.wireOp",EDGE,"E159"),sQuery(id+"F21.wireOp",EDGE,"E160.0.1.0"),sQuery(id+"F21.wireOp",EDGE,"E160.0.1.1"),sQuery(id+"F21.wireOp",EDGE,"E160.0.2.0"),sQuery(id+"F21.wireOp",EDGE,"E160.0.2.1"),sQuery(id+"F21.wireOp",EDGE,"E161"),sQuery(id+"F21.wireOp",EDGE,"E162"),sQuery(id+"F21.wireOp",EDGE,"E163"),sQuery(id+"F21.wireOp",EDGE,"E164"),sQuery(id+"F21.wireOp",EDGE,"E167"),sQuery(id+"F21.wireOp",EDGE,"E168"),sQuery(id+"F21.wireOp",EDGE,"E169"),sQuery(id+"F21.wireOp",EDGE,"E170.filletArc"),sQuery(id+"F21.wireOp",EDGE,"E171.filletArc"),sQuery(id+"F21.wireOp",EDGE,"E172.MirrorCS"),sQuery(id+"F21.wireOp",EDGE,"E174.MirrorCS"),sQuery(id+"F21.wireOp",EDGE,"E175.MirrorCS"),sQuery(id+"F21.wireOp",EDGE,"E176.MirrorCS"),sQuery(id+"F21.wireOp",EDGE,"E177.MirrorCS"),sQuery(id+"F21.wireOp",EDGE,"E178.MirrorCS"),sQuery(id+"F21.wireOp",EDGE,"E179.MirrorCS"),sQuery(id+"F21.wireOp",EDGE,"E180.MirrorCS"),sQuery(id+"F21.wireOp",EDGE,"E182.MirrorCS"),sQuery(id+"F21.wireOp",EDGE,"E183.MirrorCS"),sQuery(id+"F21.wireOp",EDGE,"E184.MirrorCS"),sQuery(id+"F21.wireOp",EDGE,"E185.MirrorCS"),sQuery(id+"F21.wireOp",EDGE,"E186.MirrorCS"),sQuery(id+"F21.wireOp",EDGE,"E187.MirrorCS"),sQuery(id+"F21.wireOp",EDGE,"E188.MirrorCS"),sQuery(id+"F21.wireOp",EDGE,"E189.MirrorCS"),sQuery(id+"F21.wireOp",EDGE,"E190.MirrorCS"),sQuery(id+"F21.wireOp",EDGE,"E191.MirrorCS"),sQuery(id+"F21.wireOp",EDGE,"E194.MirrorCS"),sQuery(id+"F21.wireOp",EDGE,"E195.MirrorCS"),sQuery(id+"F21.wireOp",EDGE,"E196.MirrorCS"),sQuery(id+"F21.wireOp",EDGE,"E197.MirrorCS"),sQuery(id+"F21.wireOp",EDGE,"E199.MirrorCS"),sQuery(id+"F21.wireOp",EDGE,"E201.MirrorCS"),sQuery(id+"F21.wireOp",EDGE,"E202.MirrorCS"),sQuery(id+"F21.wireOp",EDGE,"E203.MirrorCS")])],"isStart":false});
            var Q1;
            Q1=makeQuery(id+"F22.opExtrude","CAP_FACE",FACE,{"disambiguationData":[OSD([sQuery(id+"F21.wireOp",EDGE,"E150"),sQuery(id+"F21.wireOp",EDGE,"E151"),sQuery(id+"F21.wireOp",EDGE,"E152"),sQuery(id+"F21.wireOp",EDGE,"E153.filletArc"),sQuery(id+"F21.wireOp",EDGE,"E154.filletArc"),sQuery(id+"F21.wireOp",EDGE,"E155"),sQuery(id+"F21.wireOp",EDGE,"E156"),sQuery(id+"F21.wireOp",EDGE,"E157.0.1.0"),sQuery(id+"F21.wireOp",EDGE,"E157.0.1.1"),sQuery(id+"F21.wireOp",EDGE,"E157.0.2.0"),sQuery(id+"F21.wireOp",EDGE,"E157.0.2.1"),sQuery(id+"F21.wireOp",EDGE,"E158"),sQuery(id+"F21.wireOp",EDGE,"E159"),sQuery(id+"F21.wireOp",EDGE,"E160.0.1.0"),sQuery(id+"F21.wireOp",EDGE,"E160.0.1.1"),sQuery(id+"F21.wireOp",EDGE,"E160.0.2.0"),sQuery(id+"F21.wireOp",EDGE,"E160.0.2.1"),sQuery(id+"F21.wireOp",EDGE,"E161"),sQuery(id+"F21.wireOp",EDGE,"E162"),sQuery(id+"F21.wireOp",EDGE,"E163"),sQuery(id+"F21.wireOp",EDGE,"E164"),sQuery(id+"F21.wireOp",EDGE,"E167"),sQuery(id+"F21.wireOp",EDGE,"E168"),sQuery(id+"F21.wireOp",EDGE,"E169"),sQuery(id+"F21.wireOp",EDGE,"E170.filletArc"),sQuery(id+"F21.wireOp",EDGE,"E171.filletArc"),sQuery(id+"F21.wireOp",EDGE,"E172.MirrorCS"),sQuery(id+"F21.wireOp",EDGE,"E174.MirrorCS"),sQuery(id+"F21.wireOp",EDGE,"E175.MirrorCS"),sQuery(id+"F21.wireOp",EDGE,"E176.MirrorCS"),sQuery(id+"F21.wireOp",EDGE,"E177.MirrorCS"),sQuery(id+"F21.wireOp",EDGE,"E178.MirrorCS"),sQuery(id+"F21.wireOp",EDGE,"E179.MirrorCS"),sQuery(id+"F21.wireOp",EDGE,"E180.MirrorCS"),sQuery(id+"F21.wireOp",EDGE,"E182.MirrorCS"),sQuery(id+"F21.wireOp",EDGE,"E183.MirrorCS"),sQuery(id+"F21.wireOp",EDGE,"E184.MirrorCS"),sQuery(id+"F21.wireOp",EDGE,"E185.MirrorCS"),sQuery(id+"F21.wireOp",EDGE,"E186.MirrorCS"),sQuery(id+"F21.wireOp",EDGE,"E187.MirrorCS"),sQuery(id+"F21.wireOp",EDGE,"E188.MirrorCS"),sQuery(id+"F21.wireOp",EDGE,"E189.MirrorCS"),sQuery(id+"F21.wireOp",EDGE,"E190.MirrorCS"),sQuery(id+"F21.wireOp",EDGE,"E191.MirrorCS"),sQuery(id+"F21.wireOp",EDGE,"E194.MirrorCS"),sQuery(id+"F21.wireOp",EDGE,"E195.MirrorCS"),sQuery(id+"F21.wireOp",EDGE,"E196.MirrorCS"),sQuery(id+"F21.wireOp",EDGE,"E197.MirrorCS"),sQuery(id+"F21.wireOp",EDGE,"E199.MirrorCS"),sQuery(id+"F21.wireOp",EDGE,"E201.MirrorCS"),sQuery(id+"F21.wireOp",EDGE,"E202.MirrorCS"),sQuery(id+"F21.wireOp",EDGE,"E203.MirrorCS")])],"isStart":true});
            cPlane(context, id + "F23", {"entities" : qUnion([Q0, Q1]), "cplaneType" : CPlaneType.MID_PLANE, "offset" : 25 * mm, "width" : 150 * mm, "height" : 150 * mm});
        }
        {
            var Q0;
            Q0=makeQuery(id+"F1.opExtrude","SWEPT_BODY",BODY,{"disambiguationData":[OSD([sQuery(id+"F0.wireOp",EDGE,"E0"),sQuery(id+"F0.wireOp",EDGE,"E1"),sQuery(id+"F0.wireOp",EDGE,"E2"),sQuery(id+"F0.wireOp",EDGE,"E3")])]});
            var Q1;
            Q1=makeQuery(id+"F10.opExtrude","SWEPT_BODY",BODY,{"disambiguationData":[OSD([sQuery(id+"F9.wireOp",EDGE,"E39"),sQuery(id+"F9.wireOp",EDGE,"E40"),sQuery(id+"F9.wireOp",EDGE,"E41"),sQuery(id+"F9.wireOp",EDGE,"E43"),sQuery(id+"F9.wireOp",EDGE,"E44"),sQuery(id+"F9.wireOp",EDGE,"E45"),sQuery(id+"F9.wireOp",EDGE,"E46.filletArc"),sQuery(id+"F9.wireOp",EDGE,"E47.filletArc"),sQuery(id+"F9.wireOp",EDGE,"E48"),sQuery(id+"F9.wireOp",EDGE,"E49"),sQuery(id+"F9.wireOp",EDGE,"E50"),sQuery(id+"F9.wireOp",EDGE,"E51.1.0.0"),sQuery(id+"F9.wireOp",EDGE,"E51.1.0.1"),sQuery(id+"F9.wireOp",EDGE,"E51.2.0.0"),sQuery(id+"F9.wireOp",EDGE,"E51.2.0.1"),sQuery(id+"F9.wireOp",EDGE,"E52"),sQuery(id+"F9.wireOp",EDGE,"E53"),sQuery(id+"F9.wireOp",EDGE,"E54.1.0.0"),sQuery(id+"F9.wireOp",EDGE,"E54.1.0.1"),sQuery(id+"F9.wireOp",EDGE,"E54.2.0.0"),sQuery(id+"F9.wireOp",EDGE,"E54.2.0.1"),sQuery(id+"F9.wireOp",EDGE,"E55"),sQuery(id+"F9.wireOp",EDGE,"E56"),sQuery(id+"F9.wireOp",EDGE,"E57"),sQuery(id+"F9.wireOp",EDGE,"E58.filletArc"),sQuery(id+"F9.wireOp",EDGE,"E59.filletArc"),sQuery(id+"F9.wireOp",EDGE,"E61.MirrorCS"),sQuery(id+"F9.wireOp",EDGE,"E62.MirrorCS"),sQuery(id+"F9.wireOp",EDGE,"E63.MirrorCS"),sQuery(id+"F9.wireOp",EDGE,"E64.MirrorCS"),sQuery(id+"F9.wireOp",EDGE,"E65.MirrorCS"),sQuery(id+"F9.wireOp",EDGE,"E67.MirrorCS"),sQuery(id+"F9.wireOp",EDGE,"E68.MirrorCS"),sQuery(id+"F9.wireOp",EDGE,"E69.MirrorCS"),sQuery(id+"F9.wireOp",EDGE,"E70.MirrorCS"),sQuery(id+"F9.wireOp",EDGE,"E71.MirrorCS"),sQuery(id+"F9.wireOp",EDGE,"E72.MirrorCS"),sQuery(id+"F9.wireOp",EDGE,"E73.MirrorCS"),sQuery(id+"F9.wireOp",EDGE,"E74.MirrorCS"),sQuery(id+"F9.wireOp",EDGE,"E75.MirrorCS"),sQuery(id+"F9.wireOp",EDGE,"E76.MirrorCS"),sQuery(id+"F9.wireOp",EDGE,"E77.MirrorCS"),sQuery(id+"F9.wireOp",EDGE,"E78.MirrorCS"),sQuery(id+"F9.wireOp",EDGE,"E80.MirrorCS"),sQuery(id+"F9.wireOp",EDGE,"E81.MirrorCS"),sQuery(id+"F9.wireOp",EDGE,"E82.MirrorCS"),sQuery(id+"F9.wireOp",EDGE,"E83.MirrorCS"),sQuery(id+"F9.wireOp",EDGE,"E85.MirrorCS"),sQuery(id+"F9.wireOp",EDGE,"E86.MirrorCS"),sQuery(id+"F9.wireOp",EDGE,"E87.MirrorCS"),sQuery(id+"F9.wireOp",EDGE,"E88.MirrorCS"),sQuery(id+"F9.wireOp",EDGE,"E89.MirrorCS")])]});
            var Q2;
            Q2=makeQuery(id+"F18.opExtrude","SWEPT_BODY",BODY,{"disambiguationData":[OSD([sQuery(id+"F17.wireOp",EDGE,"E94"),sQuery(id+"F17.wireOp",EDGE,"E95"),sQuery(id+"F17.wireOp",EDGE,"E96"),sQuery(id+"F17.wireOp",EDGE,"E97.filletArc"),sQuery(id+"F17.wireOp",EDGE,"E98.filletArc"),sQuery(id+"F17.wireOp",EDGE,"E99"),sQuery(id+"F17.wireOp",EDGE,"E100"),sQuery(id+"F17.wireOp",EDGE,"E101.1.0.0"),sQuery(id+"F17.wireOp",EDGE,"E101.1.0.1"),sQuery(id+"F17.wireOp",EDGE,"E102"),sQuery(id+"F17.wireOp",EDGE,"E103"),sQuery(id+"F17.wireOp",EDGE,"E104.1.0.0"),sQuery(id+"F17.wireOp",EDGE,"E104.1.0.1"),sQuery(id+"F17.wireOp",EDGE,"E105"),sQuery(id+"F17.wireOp",EDGE,"E106"),sQuery(id+"F17.wireOp",EDGE,"E107"),sQuery(id+"F17.wireOp",EDGE,"E108.filletArc"),sQuery(id+"F17.wireOp",EDGE,"E109.filletArc"),sQuery(id+"F17.wireOp",EDGE,"E113.MirrorCS"),sQuery(id+"F17.wireOp",EDGE,"E114.MirrorCS"),sQuery(id+"F17.wireOp",EDGE,"E116.MirrorCS"),sQuery(id+"F17.wireOp",EDGE,"E117.MirrorCS"),sQuery(id+"F17.wireOp",EDGE,"E118.MirrorCS"),sQuery(id+"F17.wireOp",EDGE,"E119.MirrorCS"),sQuery(id+"F17.wireOp",EDGE,"E120.MirrorCS"),sQuery(id+"F17.wireOp",EDGE,"E121.MirrorCS"),sQuery(id+"F17.wireOp",EDGE,"E124.MirrorCS"),sQuery(id+"F17.wireOp",EDGE,"E125.MirrorCS"),sQuery(id+"F17.wireOp",EDGE,"E127.MirrorCS"),sQuery(id+"F17.wireOp",EDGE,"E128.MirrorCS"),sQuery(id+"F17.wireOp",EDGE,"E129.MirrorCS"),sQuery(id+"F17.wireOp",EDGE,"E130.MirrorCS"),sQuery(id+"F17.wireOp",EDGE,"E134.MirrorCS"),sQuery(id+"F17.wireOp",EDGE,"E135.MirrorCS"),sQuery(id+"F17.wireOp",EDGE,"E136.MirrorCS"),sQuery(id+"F17.wireOp",EDGE,"E137.MirrorCS"),sQuery(id+"F17.wireOp",EDGE,"E138"),sQuery(id+"F17.wireOp",EDGE,"E139"),sQuery(id+"F17.wireOp",EDGE,"E140"),sQuery(id+"F17.wireOp",EDGE,"E141.trimOffspring"),sQuery(id+"F17.wireOp",EDGE,"E142.MirrorCS"),sQuery(id+"F17.wireOp",EDGE,"E143.MirrorCS"),sQuery(id+"F17.wireOp",EDGE,"E144.MirrorCS"),sQuery(id+"F17.wireOp",EDGE,"E145.trimOffspring")])]});
            var Q3;
            Q3=makeQuery(id+"F12.opPattern","COPY",BODY,{"derivedFrom":makeQuery(id+"F1.opExtrude","SWEPT_BODY",BODY,{"disambiguationData":[OSD([sQuery(id+"F0.wireOp",EDGE,"E0"),sQuery(id+"F0.wireOp",EDGE,"E1"),sQuery(id+"F0.wireOp",EDGE,"E2"),sQuery(id+"F0.wireOp",EDGE,"E3")])]}),"instanceName":"1"});
            var Q4;
            Q4=qCreatedBy(id+"F23.planeOp",FACE);
            mirror(context, id + "F24", {"entities" : qUnion([Q0, Q1, Q2, Q3]), "mirrorPlane" : qUnion([Q4])});
        }
        {
            var Q0;
            Q0=makeQuery(id+"F22.opExtrude","SWEPT_FACE",FACE,{"disambiguationData":[OSD([sQuery(id+"F21.wireOp",EDGE,"E151")])]});
            var Q1;
            Q1=makeQuery(id+"F22.opExtrude","SWEPT_FACE",FACE,{"disambiguationData":[OSD([sQuery(id+"F21.wireOp",EDGE,"E197.MirrorCS")])]});
            cPlane(context, id + "F25", {"entities" : qUnion([Q0, Q1]), "cplaneType" : CPlaneType.MID_PLANE, "offset" : 25 * mm, "width" : 150 * mm, "height" : 150 * mm});
        }
        {
            var Q0;
            Q0=qCreatedBy(id+"F25.planeOp",FACE);
            var sketch = newSketch(context, id + "F26", { "sketchPlane" : qUnion([Q0])});
            skLineSegment(sketch, "E206", {"start": v(-578.85, 1052) * mm, "end": v(-578.85, 982) * mm});
            skLineSegment(sketch, "E207", {"start": v(-578.85, 982) * mm, "end": v(-28.85, 982) * mm});
            skLineSegment(sketch, "E208", {"start": v(-28.85, 982) * mm, "end": v(-28.85, 1052) * mm});
            skLineSegment(sketch, "E209", {"start": v(-28.85, 1052) * mm, "end": v(-32.85, 1052) * mm});
            skLineSegment(sketch, "E210", {"start": v(-32.85, 1052) * mm, "end": v(-32.85, 986) * mm});
            skLineSegment(sketch, "E211", {"start": v(-32.85, 986) * mm, "end": v(-574.85, 986) * mm});
            skLineSegment(sketch, "E212", {"start": v(-574.85, 986) * mm, "end": v(-574.85, 1052) * mm});
            skLineSegment(sketch, "E213", {"start": v(-574.85, 1052) * mm, "end": v(-578.85, 1052) * mm});
            skLineSegment(sketch, "E214", {"start": v(-303.85, 982) * mm, "end": v(-303.85, 1008.36) * mm, "construction": true});
            skSolve(sketch);
        }
        {
            var Q0;
            Q0 = qSketchRegion(id + "F26", true);
            extrude(context, id + "F27", {"entities" : qUnion([Q0]), "endBound" : BoundingType.SYMMETRIC, "depth" : 40 * mm, "offsetDistance" : 25 * mm});
        }
        {
            var Q0;
            Q0=makeQuery(id+"F27.opExtrude","CAP_EDGE",EDGE,{"disambiguationData":[OSD([sQuery(id+"F26.wireOp",EDGE,"E213")])],"isStart":false});
            var Q1;
            Q1=makeQuery(id+"F27.opExtrude","CAP_EDGE",EDGE,{"disambiguationData":[OSD([sQuery(id+"F26.wireOp",EDGE,"E213")])],"isStart":true});
            var Q2;
            Q2=makeQuery(id+"F27.opExtrude","CAP_EDGE",EDGE,{"disambiguationData":[OSD([sQuery(id+"F26.wireOp",EDGE,"E209")])],"isStart":false});
            var Q3;
            Q3=makeQuery(id+"F27.opExtrude","CAP_EDGE",EDGE,{"disambiguationData":[OSD([sQuery(id+"F26.wireOp",EDGE,"E209")])],"isStart":true});
            fillet(context, id + "F28", {"entities" : qUnion([Q0, Q1, Q2, Q3]), "radius" : 20 * mm, "tangentPropagation" : true, "allowEdgeOverflow" : false});
        }
        {
            var Q0;
            Q0=qCreatedBy(id+"F23.planeOp",FACE);
            var sketch = newSketch(context, id + "F29", { "sketchPlane" : qUnion([Q0])});
            skCircle(sketch, "E215", {"center": v(-293.12, 1032) * mm, "radius": 6.25 * mm});
            skSolve(sketch);
        }
        {
            var Q0;
            Q0=makeQuery(id+"F29.imprint","IMPRINT",FACE,{"disambiguationData":[TD([[makeQuery(id+"F29.imprint","IMPRINT",EDGE,{"derivedFrom":sQuery(id+"F29.wireOp",EDGE,"E215")}),1.0]])]});
            var Q1;
            Q1=makeQuery(id+"F27.opExtrude","SWEPT_FACE",FACE,{"disambiguationData":[OSD([sQuery(id+"F26.wireOp",EDGE,"E208")])]});
            var Q2;
            Q2=makeQuery(id+"F27.opExtrude","SWEPT_FACE",FACE,{"disambiguationData":[OSD([sQuery(id+"F26.wireOp",EDGE,"E206")])]});
            extrude(context, id + "F30", {"entities" : qUnion([Q0]), "operationType" : NewBodyOperationType.REMOVE, "endBound" : BoundingType.UP_TO_SURFACE, "oppositeDirection" : true, "depth" : 25 * mm, "endBoundEntityFace" : qUnion([Q1]), "offsetDistance" : 25 * mm, "hasSecondDirection" : true, "secondDirectionBound" : SecondDirectionBoundingType.UP_TO_SURFACE, "secondDirectionOppositeDirection" : false, "secondDirectionDepth" : 25 * mm, "secondDirectionBoundEntityFace" : qUnion([Q2])});
        }
        {
            var Q0;
            Q0=qCreatedBy(id+"F23.planeOp",FACE);
            var sketch = newSketch(context, id + "F31", { "sketchPlane" : qUnion([Q0])});
            skCircle(sketch, "E216", {"center": v(-293.12, 1032) * mm, "radius": 5.9 * mm});
            skSolve(sketch);
        }
        {
            var Q0;
            Q0 = qSketchRegion(id + "F31", true);
            extrude(context, id + "F32", {"entities" : qUnion([Q0]), "endBound" : BoundingType.SYMMETRIC, "depth" : 600 * mm, "offsetDistance" : 25 * mm});
        }
        {
            var Q0;
            Q0=makeQuery(id+"F32.opExtrude","CAP_EDGE",EDGE,{"disambiguationData":[OSD([sQuery(id+"F31.wireOp",EDGE,"E216")])],"isStart":false});
            var Q1;
            Q1=makeQuery(id+"F32.opExtrude","CAP_EDGE",EDGE,{"disambiguationData":[OSD([sQuery(id+"F31.wireOp",EDGE,"E216")])],"isStart":true});
            chamfer(context, id + "F33", {"entities" : qUnion([Q0, Q1]), "width" : 2 * mm, "tangentPropagation" : true});
        }
        {
            var Q0;
            Q0=qCreatedBy(id+"F23.planeOp",FACE);
            var sketch = newSketch(context, id + "F34", { "sketchPlane" : qUnion([Q0])});
            skCircle(sketch, "E217", {"center": v(-293.12, 1032) * mm, "radius": 30 * mm});
            skCircle(sketch, "E218", {"center": v(-293.12, 1032) * mm, "radius": 6.25 * mm});
            skSolve(sketch);
        }
        {
            var Q0;
            Q0 = qSketchRegion(id + "F34", true);
            extrude(context, id + "F35", {"entities" : qUnion([Q0]), "endBound" : BoundingType.SYMMETRIC, "depth" : 520 * mm, "offsetDistance" : 25 * mm});
        }
        {
            var Q0;
            Q0=makeQuery(id+"F35.opExtrude","CAP_EDGE",EDGE,{"disambiguationData":[OSD([sQuery(id+"F34.wireOp",EDGE,"E217")])],"isStart":true});
            var Q1;
            Q1=makeQuery(id+"F35.opExtrude","CAP_EDGE",EDGE,{"disambiguationData":[OSD([sQuery(id+"F34.wireOp",EDGE,"E217")])],"isStart":false});
            chamfer(context, id + "F36", {"entities" : qUnion([Q0, Q1]), "width" : 5 * mm, "tangentPropagation" : true});
        }
        {
            var Q0;
            Q0=qCreatedBy(id+"F23.planeOp",FACE);
            var sketch = newSketch(context, id + "F37", { "sketchPlane" : qUnion([Q0])});
            skLineSegment(sketch, "E219", {"start": v(-110.84, 192.21) * mm, "end": v(-99.36, 164.5) * mm, "construction": true});
            skPoint(sketch, "E220.visualSharp", {"position": v(-278.23, 137.13) * mm});
            skArc(sketch, "E220.filletArc", {"start": v(-130.57, 184.04) * mm, "mid": v(-134.63, 179.98) * mm, "end": v(-134.63, 174.24) * mm});
            skLineSegment(sketch, "E221", {"start": v(-131.38, 166.4) * mm, "end": v(-131.1, 166.5) * mm});
            skLineSegment(sketch, "E222", {"start": v(-131.1, 166.5) * mm, "end": v(-125.74, 153.57) * mm});
            skLineSegment(sketch, "E223.trimOffspring", {"start": v(-131.38, 166.4) * mm, "end": v(-134.63, 174.24) * mm});
            skLineSegment(sketch, "E224", {"start": v(-130.57, 184.04) * mm, "end": v(-129.26, 183.5) * mm});
            skLineSegment(sketch, "E225", {"start": v(-129.26, 183.5) * mm, "end": v(-128.72, 184.8) * mm});
            skLineSegment(sketch, "E226", {"start": v(-128.72, 184.8) * mm, "end": v(-127.41, 184.27) * mm});
            skLineSegment(sketch, "E227", {"start": v(-127.41, 184.27) * mm, "end": v(-126.87, 185.57) * mm});
            skLineSegment(sketch, "E228.trimOffspring", {"start": v(-125.03, 186.34) * mm, "end": v(-110.84, 192.21) * mm});
            skLineSegment(sketch, "E229", {"start": v(-126.87, 185.57) * mm, "end": v(-125.57, 185.03) * mm});
            skLineSegment(sketch, "E230", {"start": v(-125.57, 185.03) * mm, "end": v(-125.03, 186.34) * mm});
            skLineSegment(sketch, "E231", {"start": v(-130.57, 184.04) * mm, "end": v(-125.03, 186.34) * mm, "construction": true});
            skLineSegment(sketch, "E232", {"start": v(-99.36, 164.5) * mm, "end": v(-125.74, 153.57) * mm, "construction": true});
            skLineSegment(sketch, "E233", {"start": v(-109.73, 189.53) * mm, "end": v(-129.55, 181.33) * mm});
            skLineSegment(sketch, "E234", {"start": v(-131.99, 175.45) * mm, "end": v(-123.34, 154.57) * mm});
            skPoint(sketch, "E235.visualSharp", {"position": v(-133.7, 179.6) * mm});
            skArc(sketch, "E235.filletArc", {"start": v(-129.55, 181.33) * mm, "mid": v(-131.99, 178.89) * mm, "end": v(-131.99, 175.45) * mm});
            skLineSegment(sketch, "E236.MirrorCS", {"start": v(-93.5, 198.31) * mm, "end": v(-94.81, 198.85) * mm});
            skLineSegment(sketch, "E237.MirrorCS", {"start": v(-94.81, 198.85) * mm, "end": v(-95.36, 197.55) * mm});
            skLineSegment(sketch, "E238.MirrorCS", {"start": v(-91.12, 200.38) * mm, "end": v(-91.66, 199.08) * mm});
            skLineSegment(sketch, "E239.MirrorCS", {"start": v(-95.36, 197.55) * mm, "end": v(-96.66, 198.09) * mm});
            skLineSegment(sketch, "E240.MirrorCS", {"start": v(-91.66, 199.08) * mm, "end": v(-92.97, 199.62) * mm});
            skLineSegment(sketch, "E241.MirrorCS", {"start": v(-78.07, 188.47) * mm, "end": v(-78.34, 188.36) * mm});
            skLineSegment(sketch, "E242.MirrorCS", {"start": v(-91.12, 200.38) * mm, "end": v(-96.66, 198.09) * mm, "construction": true});
            skLineSegment(sketch, "E243.MirrorCS", {"start": v(-92.97, 199.62) * mm, "end": v(-93.5, 198.31) * mm});
            skArc(sketch, "E244.MirrorCS", {"start": v(-91.12, 200.38) * mm, "mid": v(-85.38, 200.38) * mm, "end": v(-81.32, 196.32) * mm});
            skArc(sketch, "E245.MirrorCS", {"start": v(-89.92, 197.74) * mm, "mid": v(-86.47, 197.74) * mm, "end": v(-84.04, 195.3) * mm});
            skPoint(sketch, "E246.MirrorP", {"position": v(46.47, 271.62) * mm});
            skPoint(sketch, "E247.MirrorP", {"position": v(-85.76, 199.46) * mm});
            skLineSegment(sketch, "E248.MirrorCS", {"start": v(-96.66, 198.09) * mm, "end": v(-110.84, 192.21) * mm});
            skLineSegment(sketch, "E249.MirrorCS", {"start": v(-78.34, 188.36) * mm, "end": v(-72.99, 175.42) * mm});
            skLineSegment(sketch, "E250.MirrorCS", {"start": v(-84.04, 195.3) * mm, "end": v(-75.39, 174.43) * mm});
            skLineSegment(sketch, "E251.MirrorCS", {"start": v(-78.07, 188.47) * mm, "end": v(-81.32, 196.32) * mm});
            skLineSegment(sketch, "E252.MirrorCS", {"start": v(-109.73, 189.53) * mm, "end": v(-89.92, 197.74) * mm});
            skLineSegment(sketch, "E253.MirrorCS", {"start": v(-70, 144.19) * mm, "end": v(-71.31, 144.73) * mm});
            skLineSegment(sketch, "E254.MirrorCS", {"start": v(-67.35, 162.6) * mm, "end": v(-67.63, 162.49) * mm});
            skLineSegment(sketch, "E255.MirrorCS", {"start": v(-107.6, 128.61) * mm, "end": v(-107.07, 129.92) * mm});
            skLineSegment(sketch, "E256.MirrorCS", {"start": v(-107.07, 129.92) * mm, "end": v(-105.76, 129.38) * mm});
            skLineSegment(sketch, "E257.MirrorCS", {"start": v(-68.16, 144.95) * mm, "end": v(-69.47, 145.5) * mm});
            skLineSegment(sketch, "E258.MirrorCS", {"start": v(-105.22, 130.68) * mm, "end": v(-103.91, 130.14) * mm});
            skLineSegment(sketch, "E259.MirrorCS", {"start": v(-120.66, 140.52) * mm, "end": v(-120.38, 140.64) * mm});
            skLineSegment(sketch, "E260.MirrorCS", {"start": v(-69.47, 145.5) * mm, "end": v(-70, 144.19) * mm});
            skLineSegment(sketch, "E261.MirrorCS", {"start": v(-107.6, 128.61) * mm, "end": v(-102.06, 130.9) * mm, "construction": true});
            skLineSegment(sketch, "E262.MirrorCS", {"start": v(-103.91, 130.14) * mm, "end": v(-103.37, 131.45) * mm});
            skLineSegment(sketch, "E263.MirrorCS", {"start": v(-105.76, 129.38) * mm, "end": v(-105.22, 130.68) * mm});
            skLineSegment(sketch, "E264.MirrorCS", {"start": v(-71.85, 143.42) * mm, "end": v(-73.16, 143.96) * mm});
            skLineSegment(sketch, "E265.MirrorCS", {"start": v(-68.16, 144.95) * mm, "end": v(-73.7, 142.65) * mm, "construction": true});
            skLineSegment(sketch, "E266.MirrorCS", {"start": v(-73.16, 143.96) * mm, "end": v(-73.7, 142.65) * mm});
            skLineSegment(sketch, "E267.MirrorCS", {"start": v(-103.37, 131.45) * mm, "end": v(-102.06, 130.9) * mm});
            skLineSegment(sketch, "E268.MirrorCS", {"start": v(-71.31, 144.73) * mm, "end": v(-71.85, 143.42) * mm});
            skArc(sketch, "E269.MirrorCS", {"start": v(-69.18, 147.67) * mm, "mid": v(-66.74, 150.1) * mm, "end": v(-66.74, 153.55) * mm});
            skArc(sketch, "E270.MirrorCS", {"start": v(-108.81, 131.25) * mm, "mid": v(-112.25, 131.25) * mm, "end": v(-114.69, 133.69) * mm});
            skArc(sketch, "E271.MirrorCS", {"start": v(-68.16, 144.95) * mm, "mid": v(-64.1, 149) * mm, "end": v(-64.1, 154.75) * mm});
            skLineSegment(sketch, "E272.MirrorCS", {"start": v(-120.66, 140.52) * mm, "end": v(-117.4, 132.67) * mm});
            skArc(sketch, "E273.MirrorCS", {"start": v(-107.6, 128.61) * mm, "mid": v(-113.35, 128.61) * mm, "end": v(-117.4, 132.67) * mm});
            skLineSegment(sketch, "E274.MirrorCS", {"start": v(-114.69, 133.69) * mm, "end": v(-123.34, 154.57) * mm});
            skPoint(sketch, "E275.MirrorP", {"position": v(-112.97, 129.53) * mm});
            skPoint(sketch, "E276.MirrorP", {"position": v(-65.02, 149.4) * mm});
            skLineSegment(sketch, "E277.MirrorCS", {"start": v(-102.06, 130.9) * mm, "end": v(-87.88, 136.78) * mm});
            skLineSegment(sketch, "E278.MirrorCS", {"start": v(-89, 139.46) * mm, "end": v(-69.18, 147.67) * mm});
            skPoint(sketch, "E279.MirrorP", {"position": v(-245.2, 57.37) * mm});
            skPoint(sketch, "E280.MirrorP", {"position": v(79.5, 191.87) * mm});
            skLineSegment(sketch, "E281.MirrorCS", {"start": v(-120.38, 140.64) * mm, "end": v(-125.74, 153.57) * mm});
            skLineSegment(sketch, "E282.MirrorCS", {"start": v(-87.88, 136.78) * mm, "end": v(-99.36, 164.5) * mm, "construction": true});
            skLineSegment(sketch, "E283.MirrorCS", {"start": v(-67.63, 162.49) * mm, "end": v(-72.99, 175.42) * mm});
            skLineSegment(sketch, "E284.MirrorCS", {"start": v(-89, 139.46) * mm, "end": v(-108.81, 131.25) * mm});
            skLineSegment(sketch, "E285.MirrorCS", {"start": v(-73.7, 142.65) * mm, "end": v(-87.88, 136.78) * mm});
            skLineSegment(sketch, "E286.MirrorCS", {"start": v(-67.35, 162.6) * mm, "end": v(-64.1, 154.75) * mm});
            skLineSegment(sketch, "E287.MirrorCS", {"start": v(-66.74, 153.55) * mm, "end": v(-75.39, 174.43) * mm});
            skSolve(sketch);
        }
        {
            var Q0;
            Q0 = qSketchRegion(id + "F37", true);
            var Q1;
            Q1=makeQuery(id+"F1.opExtrude","CAP_FACE",FACE,{"disambiguationData":[OSD([sQuery(id+"F0.wireOp",EDGE,"E0"),sQuery(id+"F0.wireOp",EDGE,"E1"),sQuery(id+"F0.wireOp",EDGE,"E2"),sQuery(id+"F0.wireOp",EDGE,"E3")])],"isStart":false});
            var Q2;
            Q2=makeQuery(id+"F24.opPattern","COPY",FACE,{"derivedFrom":makeQuery(id+"F1.opExtrude","CAP_FACE",FACE,{"disambiguationData":[OSD([sQuery(id+"F0.wireOp",EDGE,"E0"),sQuery(id+"F0.wireOp",EDGE,"E1"),sQuery(id+"F0.wireOp",EDGE,"E2"),sQuery(id+"F0.wireOp",EDGE,"E3")])],"isStart":false}),"instanceName":"1"});
            extrude(context, id + "F38", {"entities" : qUnion([Q0]), "endBound" : BoundingType.UP_TO_SURFACE, "oppositeDirection" : true, "depth" : 25 * mm, "endBoundEntityFace" : qUnion([Q1]), "offsetDistance" : 25 * mm, "hasSecondDirection" : true, "secondDirectionBound" : SecondDirectionBoundingType.UP_TO_SURFACE, "secondDirectionOppositeDirection" : false, "secondDirectionDepth" : 25 * mm, "secondDirectionBoundEntityFace" : qUnion([Q2])});
        }
        {
            var Q0;
            Q0=makeQuery(id+"F38.opExtrude","SWEPT_FACE",FACE,{"disambiguationData":[OSD([sQuery(id+"F37.wireOp",EDGE,"E228.trimOffspring"),sQuery(id+"F37.wireOp",EDGE,"E248.MirrorCS")])]});
            cPlane(context, id + "F39", {"entities" : qUnion([Q0]), "cplaneType" : CPlaneType.OFFSET, "offset" : 120 * mm, "width" : 150 * mm, "height" : 150 * mm});
        }
        {
            var Q0;
            Q0=makeQuery(id+"F38.opExtrude","SWEPT_BODY",BODY,{"disambiguationData":[OSD([sQuery(id+"F37.wireOp",EDGE,"E220.filletArc"),sQuery(id+"F37.wireOp",EDGE,"E221"),sQuery(id+"F37.wireOp",EDGE,"E222"),sQuery(id+"F37.wireOp",EDGE,"E223.trimOffspring"),sQuery(id+"F37.wireOp",EDGE,"E224"),sQuery(id+"F37.wireOp",EDGE,"E225"),sQuery(id+"F37.wireOp",EDGE,"E226"),sQuery(id+"F37.wireOp",EDGE,"E227"),sQuery(id+"F37.wireOp",EDGE,"E228.trimOffspring"),sQuery(id+"F37.wireOp",EDGE,"E229"),sQuery(id+"F37.wireOp",EDGE,"E230"),sQuery(id+"F37.wireOp",EDGE,"E233"),sQuery(id+"F37.wireOp",EDGE,"E234"),sQuery(id+"F37.wireOp",EDGE,"E235.filletArc"),sQuery(id+"F37.wireOp",EDGE,"E236.MirrorCS"),sQuery(id+"F37.wireOp",EDGE,"E237.MirrorCS"),sQuery(id+"F37.wireOp",EDGE,"E238.MirrorCS"),sQuery(id+"F37.wireOp",EDGE,"E239.MirrorCS"),sQuery(id+"F37.wireOp",EDGE,"E240.MirrorCS"),sQuery(id+"F37.wireOp",EDGE,"E241.MirrorCS"),sQuery(id+"F37.wireOp",EDGE,"E243.MirrorCS"),sQuery(id+"F37.wireOp",EDGE,"E244.MirrorCS"),sQuery(id+"F37.wireOp",EDGE,"E245.MirrorCS"),sQuery(id+"F37.wireOp",EDGE,"E248.MirrorCS"),sQuery(id+"F37.wireOp",EDGE,"E249.MirrorCS"),sQuery(id+"F37.wireOp",EDGE,"E250.MirrorCS"),sQuery(id+"F37.wireOp",EDGE,"E251.MirrorCS"),sQuery(id+"F37.wireOp",EDGE,"E252.MirrorCS"),sQuery(id+"F37.wireOp",EDGE,"E253.MirrorCS"),sQuery(id+"F37.wireOp",EDGE,"E254.MirrorCS"),sQuery(id+"F37.wireOp",EDGE,"E255.MirrorCS"),sQuery(id+"F37.wireOp",EDGE,"E256.MirrorCS"),sQuery(id+"F37.wireOp",EDGE,"E257.MirrorCS"),sQuery(id+"F37.wireOp",EDGE,"E258.MirrorCS"),sQuery(id+"F37.wireOp",EDGE,"E259.MirrorCS"),sQuery(id+"F37.wireOp",EDGE,"E260.MirrorCS"),sQuery(id+"F37.wireOp",EDGE,"E262.MirrorCS"),sQuery(id+"F37.wireOp",EDGE,"E263.MirrorCS"),sQuery(id+"F37.wireOp",EDGE,"E264.MirrorCS"),sQuery(id+"F37.wireOp",EDGE,"E266.MirrorCS"),sQuery(id+"F37.wireOp",EDGE,"E267.MirrorCS"),sQuery(id+"F37.wireOp",EDGE,"E268.MirrorCS"),sQuery(id+"F37.wireOp",EDGE,"E269.MirrorCS"),sQuery(id+"F37.wireOp",EDGE,"E270.MirrorCS"),sQuery(id+"F37.wireOp",EDGE,"E271.MirrorCS"),sQuery(id+"F37.wireOp",EDGE,"E272.MirrorCS"),sQuery(id+"F37.wireOp",EDGE,"E273.MirrorCS"),sQuery(id+"F37.wireOp",EDGE,"E274.MirrorCS"),sQuery(id+"F37.wireOp",EDGE,"E277.MirrorCS"),sQuery(id+"F37.wireOp",EDGE,"E278.MirrorCS"),sQuery(id+"F37.wireOp",EDGE,"E281.MirrorCS"),sQuery(id+"F37.wireOp",EDGE,"E283.MirrorCS"),sQuery(id+"F37.wireOp",EDGE,"E284.MirrorCS"),sQuery(id+"F37.wireOp",EDGE,"E285.MirrorCS"),sQuery(id+"F37.wireOp",EDGE,"E286.MirrorCS"),sQuery(id+"F37.wireOp",EDGE,"E287.MirrorCS")])]});
            var Q1;
            Q1=qCreatedBy(id+"F39.planeOp",FACE);
            mirror(context, id + "F40", {"entities" : qUnion([Q0]), "mirrorPlane" : qUnion([Q1])});
        }
        {
            var Q0;
            Q0=makeQuery(id+"F40.opPattern","COPY",BODY,{"derivedFrom":makeQuery(id+"F38.opExtrude","SWEPT_BODY",BODY,{"disambiguationData":[OSD([sQuery(id+"F37.wireOp",EDGE,"E220.filletArc"),sQuery(id+"F37.wireOp",EDGE,"E221"),sQuery(id+"F37.wireOp",EDGE,"E222"),sQuery(id+"F37.wireOp",EDGE,"E223.trimOffspring"),sQuery(id+"F37.wireOp",EDGE,"E224"),sQuery(id+"F37.wireOp",EDGE,"E225"),sQuery(id+"F37.wireOp",EDGE,"E226"),sQuery(id+"F37.wireOp",EDGE,"E227"),sQuery(id+"F37.wireOp",EDGE,"E228.trimOffspring"),sQuery(id+"F37.wireOp",EDGE,"E229"),sQuery(id+"F37.wireOp",EDGE,"E230"),sQuery(id+"F37.wireOp",EDGE,"E233"),sQuery(id+"F37.wireOp",EDGE,"E234"),sQuery(id+"F37.wireOp",EDGE,"E235.filletArc"),sQuery(id+"F37.wireOp",EDGE,"E236.MirrorCS"),sQuery(id+"F37.wireOp",EDGE,"E237.MirrorCS"),sQuery(id+"F37.wireOp",EDGE,"E238.MirrorCS"),sQuery(id+"F37.wireOp",EDGE,"E239.MirrorCS"),sQuery(id+"F37.wireOp",EDGE,"E240.MirrorCS"),sQuery(id+"F37.wireOp",EDGE,"E241.MirrorCS"),sQuery(id+"F37.wireOp",EDGE,"E243.MirrorCS"),sQuery(id+"F37.wireOp",EDGE,"E244.MirrorCS"),sQuery(id+"F37.wireOp",EDGE,"E245.MirrorCS"),sQuery(id+"F37.wireOp",EDGE,"E248.MirrorCS"),sQuery(id+"F37.wireOp",EDGE,"E249.MirrorCS"),sQuery(id+"F37.wireOp",EDGE,"E250.MirrorCS"),sQuery(id+"F37.wireOp",EDGE,"E251.MirrorCS"),sQuery(id+"F37.wireOp",EDGE,"E252.MirrorCS"),sQuery(id+"F37.wireOp",EDGE,"E253.MirrorCS"),sQuery(id+"F37.wireOp",EDGE,"E254.MirrorCS"),sQuery(id+"F37.wireOp",EDGE,"E255.MirrorCS"),sQuery(id+"F37.wireOp",EDGE,"E256.MirrorCS"),sQuery(id+"F37.wireOp",EDGE,"E257.MirrorCS"),sQuery(id+"F37.wireOp",EDGE,"E258.MirrorCS"),sQuery(id+"F37.wireOp",EDGE,"E259.MirrorCS"),sQuery(id+"F37.wireOp",EDGE,"E260.MirrorCS"),sQuery(id+"F37.wireOp",EDGE,"E262.MirrorCS"),sQuery(id+"F37.wireOp",EDGE,"E263.MirrorCS"),sQuery(id+"F37.wireOp",EDGE,"E264.MirrorCS"),sQuery(id+"F37.wireOp",EDGE,"E266.MirrorCS"),sQuery(id+"F37.wireOp",EDGE,"E267.MirrorCS"),sQuery(id+"F37.wireOp",EDGE,"E268.MirrorCS"),sQuery(id+"F37.wireOp",EDGE,"E269.MirrorCS"),sQuery(id+"F37.wireOp",EDGE,"E270.MirrorCS"),sQuery(id+"F37.wireOp",EDGE,"E271.MirrorCS"),sQuery(id+"F37.wireOp",EDGE,"E272.MirrorCS"),sQuery(id+"F37.wireOp",EDGE,"E273.MirrorCS"),sQuery(id+"F37.wireOp",EDGE,"E274.MirrorCS"),sQuery(id+"F37.wireOp",EDGE,"E277.MirrorCS"),sQuery(id+"F37.wireOp",EDGE,"E278.MirrorCS"),sQuery(id+"F37.wireOp",EDGE,"E281.MirrorCS"),sQuery(id+"F37.wireOp",EDGE,"E283.MirrorCS"),sQuery(id+"F37.wireOp",EDGE,"E284.MirrorCS"),sQuery(id+"F37.wireOp",EDGE,"E285.MirrorCS"),sQuery(id+"F37.wireOp",EDGE,"E286.MirrorCS"),sQuery(id+"F37.wireOp",EDGE,"E287.MirrorCS")])]}),"instanceName":"1"});
            var Q1;
            Q1=makeQuery(id+"F38.opExtrude","SWEPT_BODY",BODY,{"disambiguationData":[OSD([sQuery(id+"F37.wireOp",EDGE,"E220.filletArc"),sQuery(id+"F37.wireOp",EDGE,"E221"),sQuery(id+"F37.wireOp",EDGE,"E222"),sQuery(id+"F37.wireOp",EDGE,"E223.trimOffspring"),sQuery(id+"F37.wireOp",EDGE,"E224"),sQuery(id+"F37.wireOp",EDGE,"E225"),sQuery(id+"F37.wireOp",EDGE,"E226"),sQuery(id+"F37.wireOp",EDGE,"E227"),sQuery(id+"F37.wireOp",EDGE,"E228.trimOffspring"),sQuery(id+"F37.wireOp",EDGE,"E229"),sQuery(id+"F37.wireOp",EDGE,"E230"),sQuery(id+"F37.wireOp",EDGE,"E233"),sQuery(id+"F37.wireOp",EDGE,"E234"),sQuery(id+"F37.wireOp",EDGE,"E235.filletArc"),sQuery(id+"F37.wireOp",EDGE,"E236.MirrorCS"),sQuery(id+"F37.wireOp",EDGE,"E237.MirrorCS"),sQuery(id+"F37.wireOp",EDGE,"E238.MirrorCS"),sQuery(id+"F37.wireOp",EDGE,"E239.MirrorCS"),sQuery(id+"F37.wireOp",EDGE,"E240.MirrorCS"),sQuery(id+"F37.wireOp",EDGE,"E241.MirrorCS"),sQuery(id+"F37.wireOp",EDGE,"E243.MirrorCS"),sQuery(id+"F37.wireOp",EDGE,"E244.MirrorCS"),sQuery(id+"F37.wireOp",EDGE,"E245.MirrorCS"),sQuery(id+"F37.wireOp",EDGE,"E248.MirrorCS"),sQuery(id+"F37.wireOp",EDGE,"E249.MirrorCS"),sQuery(id+"F37.wireOp",EDGE,"E250.MirrorCS"),sQuery(id+"F37.wireOp",EDGE,"E251.MirrorCS"),sQuery(id+"F37.wireOp",EDGE,"E252.MirrorCS"),sQuery(id+"F37.wireOp",EDGE,"E253.MirrorCS"),sQuery(id+"F37.wireOp",EDGE,"E254.MirrorCS"),sQuery(id+"F37.wireOp",EDGE,"E255.MirrorCS"),sQuery(id+"F37.wireOp",EDGE,"E256.MirrorCS"),sQuery(id+"F37.wireOp",EDGE,"E257.MirrorCS"),sQuery(id+"F37.wireOp",EDGE,"E258.MirrorCS"),sQuery(id+"F37.wireOp",EDGE,"E259.MirrorCS"),sQuery(id+"F37.wireOp",EDGE,"E260.MirrorCS"),sQuery(id+"F37.wireOp",EDGE,"E262.MirrorCS"),sQuery(id+"F37.wireOp",EDGE,"E263.MirrorCS"),sQuery(id+"F37.wireOp",EDGE,"E264.MirrorCS"),sQuery(id+"F37.wireOp",EDGE,"E266.MirrorCS"),sQuery(id+"F37.wireOp",EDGE,"E267.MirrorCS"),sQuery(id+"F37.wireOp",EDGE,"E268.MirrorCS"),sQuery(id+"F37.wireOp",EDGE,"E269.MirrorCS"),sQuery(id+"F37.wireOp",EDGE,"E270.MirrorCS"),sQuery(id+"F37.wireOp",EDGE,"E271.MirrorCS"),sQuery(id+"F37.wireOp",EDGE,"E272.MirrorCS"),sQuery(id+"F37.wireOp",EDGE,"E273.MirrorCS"),sQuery(id+"F37.wireOp",EDGE,"E274.MirrorCS"),sQuery(id+"F37.wireOp",EDGE,"E277.MirrorCS"),sQuery(id+"F37.wireOp",EDGE,"E278.MirrorCS"),sQuery(id+"F37.wireOp",EDGE,"E281.MirrorCS"),sQuery(id+"F37.wireOp",EDGE,"E283.MirrorCS"),sQuery(id+"F37.wireOp",EDGE,"E284.MirrorCS"),sQuery(id+"F37.wireOp",EDGE,"E285.MirrorCS"),sQuery(id+"F37.wireOp",EDGE,"E286.MirrorCS"),sQuery(id+"F37.wireOp",EDGE,"E287.MirrorCS")])]});
            var Q2;
            Q2=qCreatedBy(id+"F25.planeOp",FACE);
            mirror(context, id + "F41", {"entities" : qUnion([Q0, Q1]), "mirrorPlane" : qUnion([Q2])});
        }
    });
